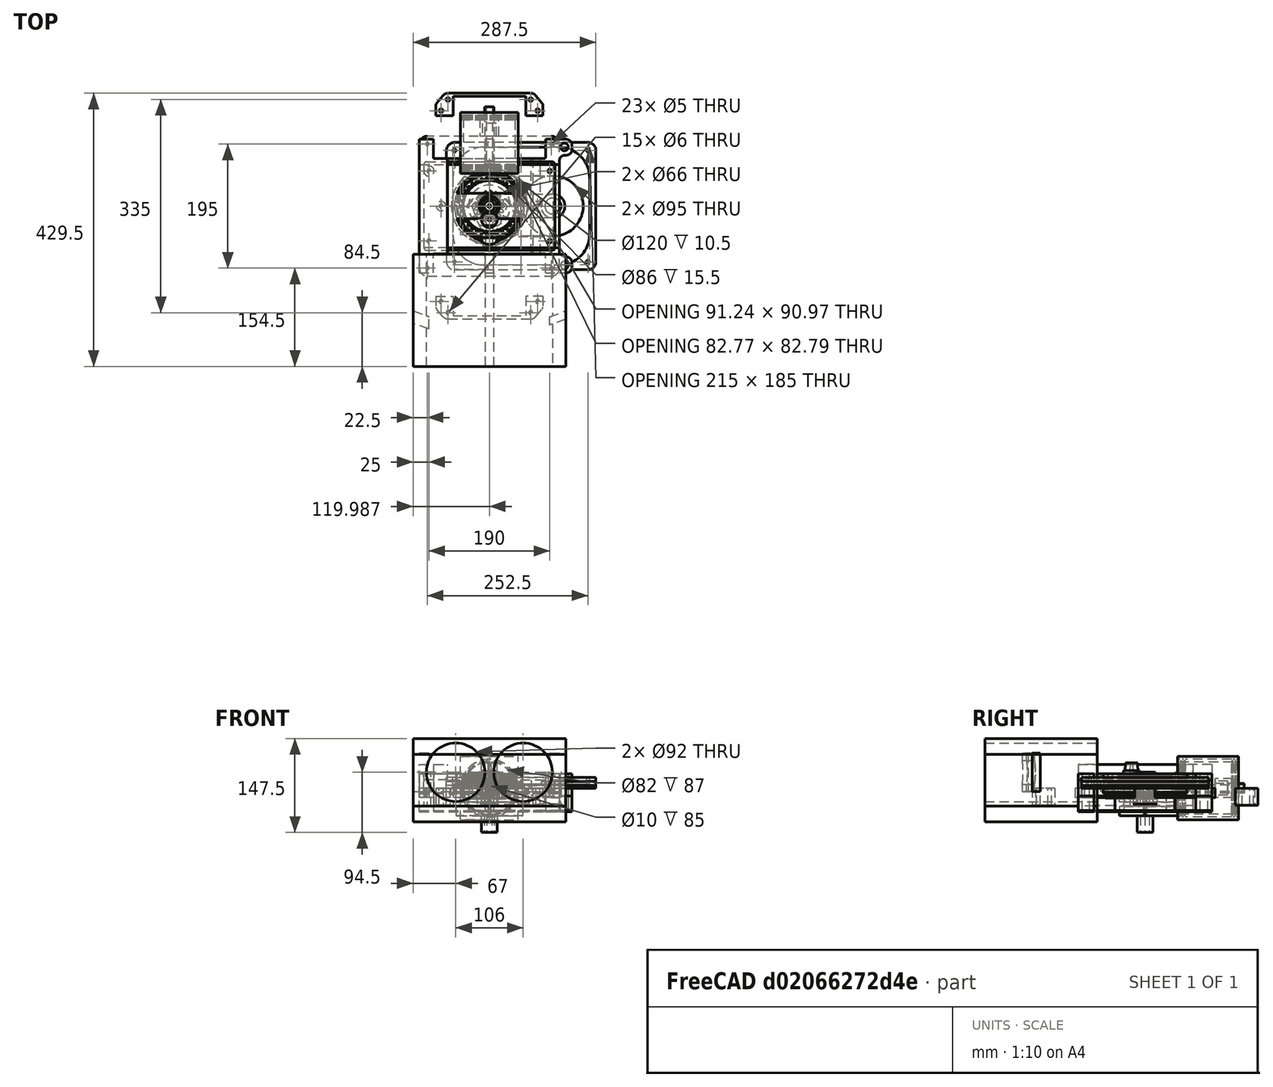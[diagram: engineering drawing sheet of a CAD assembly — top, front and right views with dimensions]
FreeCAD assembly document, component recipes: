
FREECAD ASSEMBLY — COMPONENT RECIPES ("assm4_X_at_Tusi_stirling")

This assembly document has 31 components, labeled P0..P30 below (a component is one placed body or linked part). 30 of them carry a construction recipe — the FreeCAD feature program that regenerates the part from scratch, quoted from this document or its linked companion documents; the rest are supplied as boundary geometry only. No exploded tour is included for this assembly.
COMPONENT P0 — geometry summary ("Assembly_total"; no construction recipe available for this part):
  bounding box: 312.0 x 312.0 x 138.0 mm
  tessellated surface: 110,152 triangles
  volume: 555531 mm^3 (4% of its bounding box)
  symmetry: mirror-symmetric across its x mid-plane
COMPONENT P1 — recipe-attached ("Шток_поршня", modeled in this document).
Construction recipe (the document's own serialized feature program — sketch geometry with constraints, then the solid features built on it; lengths are millimeters unless a unit is written):

FEATURE [PartDesign::CoordinateSystem] Pin
  AttacherType = Attacher::AttachEngine3D
  AttachmentSupport = -> [XY_Plane001]
  MapMode = 5
FEATURE [Sketcher::SketchObject] Sketch053
  ArcFitTolerance = 0
  AttachmentOffset = pos=(0,0,-66) rot=(0,0,1;0rad)
  AttachmentSupport = -> [XZ_Plane001]
  FullyConstrained = true
  MakeInternals = false
  MapMode = 5
  Placement = pos=(0,66,-1.47e-14) rot=(1,0,0;1.5708rad)
  sketch-geometry (2):
    g0: Circle CenterX=0 CenterY=0 CenterZ=0 NormalX=0 NormalY=0 NormalZ=1 AngleXU=0 Radius=7.5
    g1: Circle CenterX=0 CenterY=0 CenterZ=0 NormalX=0 NormalY=0 NormalZ=1 AngleXU=0 Radius=5
  constraints (4):
    c: Coincident(g0,g-1)
    c: Coincident(g1,g0)
    c: Diameter(g0) = 15
    c: Diameter(g1) = 10
FEATURE [PartDesign::Pad] Pad
  Direction = (0,-1,2e-16)
  Length = 90
  Length2 = 1
  Placement = pos=(0,0,0) rot=(1,0,0;1.5708rad)
  Profile = -> Sketch053
  ReferenceAxis = -> Sketch053 [N_Axis]
  Reversed = true
  Suppressed = false
  Type = 0
FEATURE [Sketcher::SketchObject] Sketch055
  ArcFitTolerance = 0
  AttachmentOffset = pos=(0,0,-66) rot=(0,0,1;0rad)
  AttachmentSupport = -> [XZ_Plane001]
  FullyConstrained = true
  MakeInternals = false
  MapMode = 5
  Placement = pos=(0,66,-1.47e-14) rot=(1,0,0;1.5708rad)
  sketch-geometry (2):
    g0: Circle CenterX=0 CenterY=0 CenterZ=0 NormalX=0 NormalY=0 NormalZ=1 AngleXU=0 Radius=5
    g1: Circle CenterX=0 CenterY=0 CenterZ=0 NormalX=0 NormalY=0 NormalZ=1 AngleXU=0 Radius=2
  constraints (4):
    c: Diameter(g0) = 10
    c: Coincident(g1,g0)
    c: Coincident(g0,g-1)
    c: Diameter(g1) = 4
FEATURE [PartDesign::Pad] Pad026
  BaseFeature = -> Pad
  Direction = (0,-1,2e-16)
  Length = 5
  Length2 = 17
  Placement = pos=(0,0,0) rot=(1,0,0;1.5708rad)
  Profile = -> Sketch055
  ReferenceAxis = -> Sketch055 [N_Axis]
  Reversed = true
  Suppressed = false
  Type = 4
FEATURE [Sketcher::SketchObject] Sketch085
  ArcFitTolerance = 1e-06
  AttachmentOffset = pos=(0,0,-66) rot=(0,0,1;0rad)
  AttachmentSupport = -> [XZ_Plane001]
  ExternalGeometry = -> [Pad026]
  FullyConstrained = true
  MakeInternals = false
  MapMode = 5
  Placement = pos=(0,66,-1.47e-14) rot=(1,0,0;1.5708rad)
  sketch-geometry (7):
    g0: ArcOfCircle CenterX=0 CenterY=0 CenterZ=0 NormalX=0 NormalY=0 NormalZ=1 AngleXU=0 Radius=7.5 StartAngle=2.41186 EndAngle=3.87132
    g1: LineSegment StartX=-5.59017 StartY=5 StartZ=0 EndX=5.59017 EndY=5 EndZ=0
    g2: LineSegment StartX=-5.59017 StartY=-5 StartZ=0 EndX=5.59017 EndY=-5 EndZ=0
    g3: ArcOfCircle CenterX=0 CenterY=0 CenterZ=0 NormalX=0 NormalY=0 NormalZ=1 AngleXU=0 Radius=7.5 StartAngle=5.55346 EndAngle=7.01291
    g4: LineSegment [constr] StartX=0 StartY=5 StartZ=0 EndX=0 EndY=-5 EndZ=0
    g5: LineSegment [constr] StartX=5.59017 StartY=5 StartZ=0 EndX=5.59017 EndY=-5 EndZ=0
    g6: Circle CenterX=0 CenterY=0 CenterZ=0 NormalX=0 NormalY=0 NormalZ=1 AngleXU=0 Radius=2
  constraints (20):
    c: Coincident(g0,g-1)
    c: Horizontal(g1)
    c: Horizontal(g2)
    c: Coincident(g0,g1)
    c: Coincident(g1,g3)
    c: Equal(g0,g3)
    c: Coincident(g0,g2)
    c: Coincident(g0,g3)
    c: Equal(g3,g-3)
    c: PointOnObject(g4,g-5)
    c: PointOnObject(g4,g-5)
    c: Coincident(g5,g1)
    c: Coincident(g5,g2)
    c: Vertical(g5)
    c: Equal(g4,g5)
    c: PointOnObject(g4,g-2)
    c: Coincident(g6,g0)
    c: Equal(g6,g-4)
    c: Coincident(g2,g3)
    c: Vertical(g4)
FEATURE [PartDesign::Pad] Pad046
  BaseFeature = -> Pad026
  Direction = (0,-1,2e-16)
  Length = 2
  Length2 = 10
  Placement = pos=(0,0,0) rot=(1,0,0;1.5708rad)
  Profile = -> Sketch085
  ReferenceAxis = -> Sketch085 [N_Axis]
  Refine = true
  Suppressed = false
  Type = 0
FEATURE [PartDesign::Body] Body  label="Шток_поршня"
  AllowCompound = false
  Group = -> [Pin,Sketch053,Pad,Sketch055,Pad026,Sketch085,Pad046]
  Origin = -> Origin001
  Tip = -> Pad046
COMPONENT P2 — recipe-attached ("Эксцентрик", modeled in this document).
Construction recipe (the document's own serialized feature program — sketch geometry with constraints, then the solid features built on it; lengths are millimeters unless a unit is written):

FEATURE [Sketcher::SketchObject] Sketch005
  ArcFitTolerance = 0
  AttachmentSupport = -> [XY_Plane002]
  FullyConstrained = true
  MakeInternals = false
  MapMode = 5
  expr: Constraints[1] = <<Dim_table>>.crank_dia2 + <<Dim_table>>.zazor
  expr: Constraints[26] = 10
  expr: Constraints[27] = <<Dim_table>>.ecc_dia * 0.8
  expr: Constraints[28] = <<Dim_table>>.crank_dia2 * 2
  expr: Constraints[2] = <<Dim_table>>.ecc_dia + <<Dim_table>>.roller_dia
  expr: Constraints[3] = <<Dim_table>>.crank_len
  sketch-geometry (14):
    g0: Circle CenterX=0 CenterY=-21.25 CenterZ=0 NormalX=0 NormalY=0 NormalZ=1 AngleXU=0 Radius=41.5
    g1: Circle CenterX=0 CenterY=0 CenterZ=0 NormalX=0 NormalY=0 NormalZ=1 AngleXU=0 Radius=12.75
    g2: ArcOfCircle CenterX=0 CenterY=-21.25 CenterZ=0 NormalX=0 NormalY=0 NormalZ=1 AngleXU=0 Radius=32 StartAngle=3.32205 EndAngle=4.38515
    g3: ArcOfCircle CenterX=0 CenterY=-21.25 CenterZ=0 NormalX=0 NormalY=0 NormalZ=1 AngleXU=0 Radius=32 StartAngle=5.03963 EndAngle=6.10273
    g4: LineSegment StartX=-5 StartY=-27.5681 StartZ=0 EndX=-5 EndY=-47.7641 EndZ=0
    g5: LineSegment StartX=5 StartY=-27.5681 StartZ=0 EndX=5 EndY=-47.7641 EndZ=0
    g6: ArcOfCircle CenterX=0 CenterY=0 CenterZ=0 NormalX=0 NormalY=0 NormalZ=1 AngleXU=0 Radius=25 StartAngle=3.98424 EndAngle=4.39683
    g7: ArcOfCircle CenterX=0 CenterY=0 CenterZ=0 NormalX=0 NormalY=0 NormalZ=1 AngleXU=0 Radius=25 StartAngle=5.02794 EndAngle=5.44053
    g8: ArcOfCircle CenterX=-22.6265 CenterY=-25.3779 CenterZ=0 NormalX=0 NormalY=0 NormalZ=1 AngleXU=0 Radius=9 StartAngle=0.842651 EndAngle=3.32205
    g9: ArcOfCircle CenterX=22.6265 CenterY=-25.3779 CenterZ=0 NormalX=0 NormalY=0 NormalZ=1 AngleXU=0 Radius=9 StartAngle=6.10273 EndAngle=8.58213
    g10: ArcOfCircle CenterX=-9 CenterY=-47.7641 CenterZ=0 NormalX=0 NormalY=0 NormalZ=1 AngleXU=0 Radius=4 StartAngle=4.38515 EndAngle=6.28319
    g11: ArcOfCircle CenterX=9 CenterY=-47.7641 CenterZ=0 NormalX=0 NormalY=0 NormalZ=1 AngleXU=0 Radius=4 StartAngle=3.14159 EndAngle=5.03963
    g12: ArcOfCircle CenterX=-9 CenterY=-27.5681 CenterZ=0 NormalX=0 NormalY=0 NormalZ=1 AngleXU=0 Radius=4 StartAngle=0 EndAngle=1.25524
    g13: ArcOfCircle CenterX=9 CenterY=-27.5681 CenterZ=0 NormalX=0 NormalY=0 NormalZ=1 AngleXU=0 Radius=4 StartAngle=1.88635 EndAngle=3.14159
  constraints (32):
    c: PointOnObject(g0,g-2)
    c: Diameter(g1) = 25.5
    c: Diameter(g0) = 83
    c: Distance(g1,g0) = 21.25
    c: Coincident(g1,g-1)
    c: Coincident(g2,g0)
    c: Coincident(g3,g0)
    c: Equal(g2,g3)
    c: Vertical(g4)
    c: Coincident(g6,g1)
    c: Coincident(g7,g1)
    c: Tangent(g2,g8) = -1.5708
    c: Tangent(g6,g8) = 1.5708
    c: Tangent(g7,g9) = 1.5708
    c: Tangent(g3,g9) = -1.5708
    c: Tangent(g2,g10) = -1.5708
    c: Tangent(g4,g10) = 1.5708
    c: Tangent(g5,g11) = -1.5708
    c: Tangent(g3,g11) = -1.5708
    c: Tangent(g6,g12) = 1.5708
    c: Tangent(g4,g12) = 1.5708
    c: Tangent(g5,g13) = -1.5708
    c: Tangent(g7,g13) = 1.5708
    c: Symmetric(g12,g13,g-2)
    c: Symmetric(g10,g11,g-2)
    c: Symmetric(g8,g9,g-2)
    c: DistanceX(g4,g5) = 10
    c: Diameter(g2) = 64
    c: Diameter(g6) = 50
    c: Radius(g10) = 4
    c: Equal(g10,g12)
    c: Radius(g8) = 9
FEATURE [PartDesign::CoordinateSystem] Eccentr
  AttacherType = Attacher::AttachEngine3D
  AttachmentOffset = pos=(0,0,0) rot=(0,0,1;1.5708rad)
  AttachmentSupport = -> [Sketch005]
  MapMode = 11
  Placement = pos=(0,0,0) rot=(0,0,1;3.14159rad)
FEATURE [PartDesign::Pad] Pad001
  Direction = (0,0,1)
  Length = 16.5
  Length2 = 0
  Profile = -> Sketch005
  ReferenceAxis = -> Sketch005 [N_Axis]
  Reversed = true
  Suppressed = false
  Type = 0
  expr: Length = <<Dim_table>>.ecc_hei
FEATURE [PartDesign::SubtractiveCylinder] Cylinder003
  Angle = 360
  AttacherType = Attacher::AttachEngine3D
  AttachmentOffset = pos=(0,0,-12.5) rot=(0,0,1;0rad)
  AttachmentSupport = -> [Pad001]
  BaseFeature = -> Pad001
  FirstAngle = 0
  Height = 25.2
  MapMode = 2
  Placement = pos=(0,0,-12.5) rot=(0,0,1;0rad)
  Radius = 16
  Refine = true
  SecondAngle = 0
  Suppressed = false
FEATURE [PartDesign::SubtractiveCylinder] Cylinder008
  Angle = 360
  AttacherType = Attacher::AttachEngine3D
  AttachmentOffset = pos=(23,0,-13) rot=(0,0,1;0rad)
  AttachmentSupport = -> [XY_Plane002]
  BaseFeature = -> Cylinder003
  FirstAngle = 0
  Height = 25
  MapMode = 5
  Placement = pos=(23,0,-13) rot=(0,0,1;0rad)
  Radius = 4
  Refine = true
  SecondAngle = 0
  Suppressed = false
FEATURE [PartDesign::SubtractiveCylinder] Cylinder009
  Angle = 360
  AttacherType = Attacher::AttachEngine3D
  AttachmentOffset = pos=(-23,0,-13) rot=(0,0,1;0rad)
  AttachmentSupport = -> [XY_Plane002]
  BaseFeature = -> Cylinder008
  FirstAngle = 0
  Height = 25
  MapMode = 5
  Placement = pos=(-23,0,-13) rot=(0,0,1;0rad)
  Radius = 4
  Refine = true
  SecondAngle = 0
  Suppressed = false
FEATURE [Sketcher::SketchObject] Sketch084
  ArcFitTolerance = 1e-06
  AttachmentSupport = -> [XY_Plane002]
  FullyConstrained = true
  MakeInternals = false
  MapMode = 5
  expr: Constraints[2] = <<Dim_table>>.crank_len
  expr: Constraints[3] = <<Dim_table>>.ecc_dia
  expr: Constraints[4] = <<Dim_table>>.ecc_dia * 1.2
  sketch-geometry (2):
    g0: Circle CenterX=0 CenterY=-21.25 CenterZ=0 NormalX=0 NormalY=0 NormalZ=1 AngleXU=0 Radius=40
    g1: Circle CenterX=0 CenterY=-21.25 CenterZ=0 NormalX=0 NormalY=0 NormalZ=1 AngleXU=0 Radius=48
  constraints (5):
    c: PointOnObject(g0,g-2)
    c: Coincident(g1,g0)
    c: Distance(g0,g-1) = 21.25
    c: Diameter(g0) = 80
    c: Diameter(g1) = 96
FEATURE [PartDesign::Pocket] Pocket
  BaseFeature = -> Cylinder009
  Direction = (0,0,-1)
  Length = 15.25
  Length2 = -1.25
  Placement = pos=(-23,0,-13) rot=(0,0,1;0rad)
  Profile = -> Sketch084
  ReferenceAxis = -> Sketch084 [N_Axis]
  Refine = true
  Suppressed = false
  Type = 4
FEATURE [PartDesign::Body] Body001  label="Эксцентрик"
  AllowCompound = false
  Group = -> [Sketch005,Pad001,Eccentr,Cylinder003,Cylinder008,Cylinder009,Sketch084,Pocket]
  Origin = -> Origin002
  Tip = -> Pocket
COMPONENT P3 — recipe-attached ("Ползун_рабочий", modeled in this document).
Construction recipe (the document's own serialized feature program — sketch geometry with constraints, then the solid features built on it; lengths are millimeters unless a unit is written):

FEATURE [Sketcher::SketchObject] Sketch007
  ArcFitTolerance = 0
  AttachmentSupport = -> [XY_Plane003]
  FullyConstrained = true
  MakeInternals = false
  MapMode = 5
  expr: Constraints[15] = <<Dim_table>>.ecc_dia * 1.3
  expr: Constraints[17] = <<Dim_table>>.ecc_dia * 0.8
  expr: Constraints[1] = <<Dim_table>>.ecc_dia + 2 * <<Dim_table>>.roller_dia
  sketch-geometry (15):
    g0: Circle CenterX=0 CenterY=0 CenterZ=0 NormalX=0 NormalY=0 NormalZ=1 AngleXU=0 Radius=43
    g1: ArcOfCircle CenterX=0 CenterY=0 CenterZ=0 NormalX=0 NormalY=0 NormalZ=1 AngleXU=0 Radius=52 StartAngle=1.86916 EndAngle=3.14159
    g2: ArcOfCircle CenterX=0 CenterY=0 CenterZ=0 NormalX=0 NormalY=0 NormalZ=1 AngleXU=0 Radius=52 StartAngle=0 EndAngle=1.27243
    g3: LineSegment StartX=-11.8314 StartY=53.6134 StartZ=0 EndX=-10 EndY=64 EndZ=0
    g4: LineSegment StartX=-10 StartY=64 StartZ=0 EndX=10 EndY=64 EndZ=0
    g5: LineSegment StartX=10 StartY=64 StartZ=0 EndX=11.8314 EndY=53.6134 EndZ=0
    g6: ArcOfCircle CenterX=-16.7555 CenterY=54.4817 CenterZ=0 NormalX=0 NormalY=0 NormalZ=1 AngleXU=0 Radius=5 StartAngle=5.01075 EndAngle=6.10865
    g7: ArcOfCircle CenterX=16.7555 CenterY=54.4817 CenterZ=0 NormalX=0 NormalY=0 NormalZ=1 AngleXU=0 Radius=5 StartAngle=3.31613 EndAngle=4.41403
    g8: ArcOfCircle CenterX=-2.7e-15 CenterY=2.94305e-05 CenterZ=0 NormalX=0 NormalY=0 NormalZ=1 AngleXU=0 Radius=52 StartAngle=3.14159 EndAngle=4.41403
    g9: ArcOfCircle CenterX=-16.7555 CenterY=-54.4817 CenterZ=0 NormalX=0 NormalY=0 NormalZ=1 AngleXU=0 Radius=5 StartAngle=0.174533 EndAngle=1.27243
    g10: LineSegment StartX=-11.8314 StartY=-53.6134 StartZ=0 EndX=-10 EndY=-64 EndZ=0
    g11: LineSegment StartX=-10 StartY=-64 StartZ=0 EndX=10 EndY=-64 EndZ=0
    g12: LineSegment StartX=10 StartY=-64 StartZ=0 EndX=11.8314 EndY=-53.6134 EndZ=0
    g13: ArcOfCircle CenterX=16.7555 CenterY=-54.4817 CenterZ=0 NormalX=0 NormalY=0 NormalZ=1 AngleXU=0 Radius=5 StartAngle=1.86916 EndAngle=2.96706
    g14: ArcOfCircle CenterX=-2.7e-15 CenterY=2.94305e-05 CenterZ=0 NormalX=0 NormalY=0 NormalZ=1 AngleXU=0 Radius=52 StartAngle=5.01075 EndAngle=6.28318
  constraints (36):
    c: Coincident(g0,g-1)
    c: Diameter(g0) = 86
    c: Coincident(g1,g0)
    c: Coincident(g2,g0)
    c: Equal(g1,g2)
    c: Coincident(g3,g4)
    c: Coincident(g4,g5)
    c: Tangent(g1,g6) = 1.5708
    c: Tangent(g3,g6) = -1.5708
    c: Tangent(g5,g7) = -1.5708
    c: Tangent(g2,g7) = 1.5708
    c: Symmetric(g6,g7,g-2)
    c: Symmetric(g3,g4,g-2)
    c: PointOnObject(g1,g-1)
    c: PointOnObject(g2,g-1)
    c: Diameter(g1) = 104
    c: Distance(g4,g4) = 20
    c: DistanceY(g0,g4) = 64
    c: Radius(g6) = 5
    c: Angle(g3,g-2) = 0.174533
    c: Equal(g8,g14)
    c: Coincident(g10,g11)
    c: Coincident(g11,g12)
    c: Tangent(g8,g9) = 1.5708
    c: Tangent(g10,g9) = 1.5708
    c: Tangent(g12,g13) = 1.5708
    c: Tangent(g14,g13) = 1.5708
    c: Equal(g8,g1)
    c: Equal(g13,g7)
    c: Symmetric(g9,g13,g-2)
    c: Symmetric(g11,g4,g-1)
    c: Symmetric(g10,g11,g-2)
    c: Parallel(g12,g3)
    c: Coincident(g8,g1)
    c: Coincident(g14,g2)
    c: Coincident(g8,g14)
FEATURE [PartDesign::Pad] Pad002
  Direction = (0,0,1)
  Length = 15.5
  Length2 = 10
  Midplane = true
  Profile = -> Sketch007
  ReferenceAxis = -> Sketch007 [N_Axis]
  Suppressed = false
  Type = 0
  expr: Length = <<Dim_table>>.ecc_hei - 1
FEATURE [PartDesign::CoordinateSystem] Shtok
  AttacherType = Attacher::AttachEngine3D
  AttachmentSupport = -> [Pad002]
  MapMode = 45
  Placement = pos=(-7.2e-15,2.69855e-05,-3e-16) rot=(0,0,1;0rad)
FEATURE [Sketcher::SketchObject] Sketch
  ArcFitTolerance = 1e-06
  AttachmentSupport = -> [Pad002]
  FullyConstrained = true
  MakeInternals = false
  MapMode = 5
  Placement = pos=(0,-64,0) rot=(1,0,0;1.5708rad)
  sketch-geometry (1):
    g0: Circle CenterX=0 CenterY=0 CenterZ=0 NormalX=0 NormalY=0 NormalZ=1 AngleXU=0 Radius=0.5
  constraints (2):
    c: Coincident(g0,g-1)
    c: Diameter(g0) = 1
FEATURE [PartDesign::Hole] Hole001
  BaseFeature = -> Pad002
  CustomThreadClearance = 0
  Depth = 15
  DepthType = 0
  Diameter = 11
  DrillForDepth = false
  DrillPoint = 1
  DrillPointAngle = 118
  HoleCutCountersinkAngle = 90
  HoleCutCustomValues = false
  HoleCutDepth = 0
  HoleCutDiameter = 6.1
  HoleCutType = 0
  ModelThread = false
  Profile = -> Sketch
  Refine = true
  Suppressed = false
  Tapered = false
  TaperedAngle = 90
  ThreadClass = 0
  ThreadDepth = 15
  ThreadDepthType = 0
  ThreadDirection = 0
  ThreadFit = 0
  ThreadSize = 22
  ThreadType = 2
  Threaded = false
  UseCustomThreadClearance = false
FEATURE [Sketcher::SketchObject] Sketch083
  ArcFitTolerance = 1e-06
  AttachmentSupport = -> [Hole001]
  FullyConstrained = true
  MakeInternals = false
  MapMode = 5
  Placement = pos=(0,64,0) rot=(0,0.707107,0.707107;3.14159rad)
  sketch-geometry (1):
    g0: Circle CenterX=0 CenterY=0 CenterZ=0 NormalX=0 NormalY=0 NormalZ=1 AngleXU=0 Radius=0.5
  constraints (2):
    c: Coincident(g0,g-1)
    c: Diameter(g0) = 1
FEATURE [PartDesign::Hole] Hole002
  BaseFeature = -> Hole001
  CustomThreadClearance = 0
  Depth = 15
  DepthType = 0
  Diameter = 11
  DrillForDepth = false
  DrillPoint = 1
  DrillPointAngle = 118
  HoleCutCountersinkAngle = 90
  HoleCutCustomValues = false
  HoleCutDepth = 0
  HoleCutDiameter = 6.1
  HoleCutType = 0
  ModelThread = false
  Profile = -> Sketch083
  Refine = true
  Suppressed = false
  Tapered = false
  TaperedAngle = 90
  ThreadClass = 0
  ThreadDepth = 15
  ThreadDepthType = 0
  ThreadDirection = 0
  ThreadFit = 0
  ThreadSize = 22
  ThreadType = 2
  Threaded = false
  UseCustomThreadClearance = false
FEATURE [PartDesign::Body] Body002  label="Ползун_рабочий"
  AllowCompound = false
  Group = -> [Sketch007,Pad002,Shtok,Sketch,Hole001,Sketch083,Hole002]
  Origin = -> Origin003
  Tip = -> Hole002
COMPONENT P4 — recipe-attached ("Шейка_шатунная", modeled in this document).
Construction recipe (the document's own serialized feature program — sketch geometry with constraints, then the solid features built on it; lengths are millimeters unless a unit is written):

FEATURE [Sketcher::SketchObject] Sketch004
  ArcFitTolerance = 0
  AttachmentSupport = -> [XY_Plane004]
  FullyConstrained = true
  MakeInternals = false
  MapMode = 5
  expr: Constraints[0] = <<Dim_table>>.crank_dia2
  expr: Constraints[2] = <<Dim_table>>.crank_len
  expr: Constraints[4] = <<Dim_table>>.axle_hole_dia
  sketch-geometry (2):
    g0: Circle CenterX=0 CenterY=-21.25 CenterZ=0 NormalX=0 NormalY=0 NormalZ=1 AngleXU=0 Radius=12.5
    g1: Circle CenterX=0 CenterY=-21.25 CenterZ=0 NormalX=0 NormalY=0 NormalZ=1 AngleXU=0 Radius=2.5
  constraints (5):
    c: Diameter(g0) = 25
    c: PointOnObject(g0,g-2)
    c: DistanceY(g0,g-1) = 21.25
    c: Coincident(g1,g0)
    c: Diameter(g1) = 5
FEATURE [PartDesign::Pad] Pad003
  Direction = (0,0,1)
  Length = 63
  Length2 = 0
  Profile = -> Sketch004
  ReferenceAxis = -> Sketch004 [N_Axis]
  Suppressed = false
  Type = 0
FEATURE [Sketcher::SketchObject] Sketch070
  ArcFitTolerance = 0
  AttachmentSupport = -> [Pad003]
  FullyConstrained = true
  MakeInternals = false
  MapMode = 11
  Placement = pos=(0,-21.25,63) rot=(0,0,1;1.5708rad)
  expr: Constraints[12] = <<Dim_table>>.crank_dia2
  expr: Constraints[13] = <<Dim_table>>.axle_hole_dia
  expr: Constraints[14] = 0
  expr: Constraints[3] = <<Dim_table>>.crank_dia2 * 0.8
  sketch-geometry (5):
    g0: ArcOfCircle CenterX=0 CenterY=0 CenterZ=0 NormalX=0 NormalY=0 NormalZ=1 AngleXU=0 Radius=12.5 StartAngle=0.643501 EndAngle=2.49809
    g1: ArcOfCircle CenterX=0 CenterY=0 CenterZ=0 NormalX=0 NormalY=0 NormalZ=1 AngleXU=0 Radius=12.5 StartAngle=3.78509 EndAngle=5.63968
    g2: LineSegment StartX=10 StartY=7.5 StartZ=0 EndX=10 EndY=-7.5 EndZ=0
    g3: LineSegment StartX=-10 StartY=7.5 StartZ=0 EndX=-10 EndY=-7.5 EndZ=0
    g4: Circle CenterX=0 CenterY=0 CenterZ=0 NormalX=0 NormalY=0 NormalZ=1 AngleXU=0 Radius=2.5
  constraints (15):
    c: Coincident(g2,g0)
    c: Coincident(g2,g1)
    c: Vertical(g2)
    c: DistanceX(g0,g0) = 20
    c: Coincident(g3,g0)
    c: Coincident(g3,g1)
    c: Vertical(g3)
    c: Equal(g3,g2)
    c: Equal(g1,g0)
    c: Coincident(g1,g0)
    c: Coincident(g4,g0)
    c: PointOnObject(g0,g-2)
    c: Diameter(g0) = 25
    c: Diameter(g4) = 5
    c: DistanceY(g-1,g0) = 0
FEATURE [PartDesign::Pad] Pad038
  BaseFeature = -> Pad003
  Direction = (0,0,1)
  Length = 12
  Length2 = 10
  Profile = -> Sketch070
  ReferenceAxis = -> Sketch070 [N_Axis]
  Suppressed = false
  TaperAngle = -2
  Type = 0
FEATURE [PartDesign::Body] Body003  label="Шейка_шатунная"
  AllowCompound = false
  Group = -> [Sketch004,Pad003,Sketch070,Pad038]
  Origin = -> Origin004
  Placement = pos=(0,0,-25) rot=(0,0,1;0rad)
  Tip = -> Pad038
COMPONENT P5 — recipe-attached ("Щека", modeled in this document).
Construction recipe (the document's own serialized feature program — sketch geometry with constraints, then the solid features built on it; lengths are millimeters unless a unit is written):

FEATURE [Sketcher::SketchObject] Sketch003
  ArcFitTolerance = 0
  AttachmentSupport = -> [XY_Plane005]
  FullyConstrained = true
  MakeInternals = false
  MapMode = 5
  expr: Constraints[17] = <<Dim_table>>.fillet_r
  expr: Constraints[18] = <<Dim_table>>.fillet_r
  expr: Constraints[21] = <<Dim_table>>.inter_shaft_len - <<Dim_table>>.zazor
  expr: Constraints[23] = <<Dim_table>>.axle_hole_dia
  expr: Constraints[25] = 70
  expr: Constraints[26] = <<Dim_table>>.crank_dia2 * 1.5
  expr: Constraints[27] = <<Dim_table>>.crank_len
  sketch-geometry (14):
    g0: ArcOfCircle CenterX=0 CenterY=0 CenterZ=0 NormalX=0 NormalY=0 NormalZ=1 AngleXU=0 Radius=52.5 StartAngle=0.0396143 EndAngle=3.10198
    g1: ArcOfCircle CenterX=-1.2e-15 CenterY=-21.25 CenterZ=0 NormalX=0 NormalY=0 NormalZ=1 AngleXU=0 Radius=18.75 StartAngle=3.49066 EndAngle=5.93412
    g2: LineSegment [constr] StartX=-17.6192 StartY=-27.6629 StartZ=0 EndX=17.6192 EndY=-27.6629 EndZ=0
    g3: LineSegment StartX=-50.4604 StartY=0 StartZ=0 EndX=-29.0881 EndY=0 EndZ=0
    g4: LineSegment StartX=-27.2087 StartY=-1.31596 StartZ=0 EndX=-17.6192 EndY=-27.6629 EndZ=0
    g5: LineSegment StartX=17.6192 StartY=-27.6629 StartZ=0 EndX=27.2087 EndY=-1.31596 EndZ=0
    g6: LineSegment StartX=29.0881 StartY=-7e-16 StartZ=0 EndX=50.4604 EndY=-7e-16 EndZ=0
    g7: ArcOfCircle CenterX=-29.0881 CenterY=-2 CenterZ=0 NormalX=0 NormalY=0 NormalZ=1 AngleXU=0 Radius=2 StartAngle=0.349066 EndAngle=1.5708
    g8: ArcOfCircle CenterX=29.0881 CenterY=-2 CenterZ=0 NormalX=0 NormalY=0 NormalZ=1 AngleXU=0 Radius=2 StartAngle=1.5708 EndAngle=2.79253
    g9: ArcOfCircle CenterX=50.4604 CenterY=2 CenterZ=0 NormalX=0 NormalY=0 NormalZ=1 AngleXU=0 Radius=2 StartAngle=4.71239 EndAngle=6.3228
    g10: ArcOfCircle CenterX=-50.4604 CenterY=2 CenterZ=0 NormalX=0 NormalY=0 NormalZ=1 AngleXU=0 Radius=2 StartAngle=3.10198 EndAngle=4.71239
    g11: Circle [constr] CenterX=0 CenterY=0 CenterZ=0 NormalX=0 NormalY=0 NormalZ=1 AngleXU=0 Radius=49.75
    g12: Circle CenterX=0 CenterY=0 CenterZ=0 NormalX=0 NormalY=0 NormalZ=1 AngleXU=0 Radius=2.5
    g13: Circle [constr] CenterX=-1.2e-15 CenterY=-21.25 CenterZ=0 NormalX=0 NormalY=0 NormalZ=1 AngleXU=0 Radius=2.5
  constraints (31):
    c: Coincident(g2,g1)
    c: Coincident(g2,g1)
    c: Horizontal(g2)
    c: Horizontal(g3)
    c: Horizontal(g6)
    c: Tangent(g4,g1) = -1.5708
    c: Tangent(g5,g1) = -1.5708
    c: Tangent(g3,g7) = 1.5708
    c: Tangent(g4,g7) = 1.5708
    c: Tangent(g6,g8) = 1.5708
    c: Tangent(g5,g8) = 1.5708
    c: Tangent(g6,g9) = -1.5708
    c: Tangent(g0,g9) = -1.5708
    c: Tangent(g0,g10) = -1.5708
    c: Tangent(g3,g10) = -1.5708
    c: Symmetric(g7,g8,g-2)
    c: Symmetric(g10,g9,g-2)
    c: Radius(g10) = 2
    c: Radius(g7) = 2
    c: Coincident(g0,g-1)
    c: Coincident(g11,g0)
    c: Diameter(g11) = 99.5
    c: Coincident(g12,g11)
    c: Diameter(g12) = 5
    c: Diameter(g0) = 105
    c: Angle(g5) = 1.22173
    c: Diameter(g1) = 37.5
    c: DistanceY(g1,g12) = 21.25
    c: PointOnObject(g3,g-1)
    c: Coincident(g13,g1)
    c: Equal(g13,g12)
FEATURE [PartDesign::Pad] Pad004
  Direction = (0,0,1)
  Length = 15
  Length2 = 10
  Profile = -> Sketch003
  ReferenceAxis = -> Sketch003 [N_Axis]
  Suppressed = false
  Type = 0
FEATURE [PartDesign::Body] Body004  label="Щека"
  AllowCompound = false
  Group = -> [Sketch003,Pad004]
  Origin = -> Origin005
  Placement = pos=(0,0,12.5) rot=(0,0,1;0rad)
  Tip = -> Pad004
COMPONENT P6 — recipe-attached ("Шейка коренная", modeled in this document).
Construction recipe (the document's own serialized feature program — sketch geometry with constraints, then the solid features built on it; lengths are millimeters unless a unit is written):

FEATURE [Sketcher::SketchObject] Sketch002
  ArcFitTolerance = 0
  AttachmentSupport = -> [XY_Plane006]
  FullyConstrained = true
  MakeInternals = false
  MapMode = 5
  expr: Constraints[0] = <<Dim_table>>.crank_dia1
  expr: Constraints[20] = <<Dim_table>>.hex_size
  sketch-geometry (8):
    g0: Circle CenterX=0 CenterY=0 CenterZ=0 NormalX=0 NormalY=0 NormalZ=1 AngleXU=0 Radius=12.5
    g1: LineSegment StartX=4.04145 StartY=7 StartZ=0 EndX=-4.04145 EndY=7 EndZ=0
    g2: LineSegment StartX=-4.04145 StartY=7 StartZ=0 EndX=-8.0829 EndY=0 EndZ=0
    g3: LineSegment StartX=-8.0829 StartY=0 StartZ=0 EndX=-4.04145 EndY=-7 EndZ=0
    g4: LineSegment StartX=-4.04145 StartY=-7 StartZ=0 EndX=4.04145 EndY=-7 EndZ=0
    g5: LineSegment StartX=4.04145 StartY=-7 StartZ=0 EndX=8.0829 EndY=-9e-16 EndZ=0
    g6: LineSegment StartX=8.0829 StartY=-9e-16 StartZ=0 EndX=4.04145 EndY=7 EndZ=0
    g7: Circle [constr] CenterX=0 CenterY=0 CenterZ=0 NormalX=0 NormalY=0 NormalZ=1 AngleXU=0 Radius=8.0829
  constraints (18):
    c: Diameter(g0) = 25
    c: Coincident(g1,g2)
    c: Coincident(g2,g3)
    c: Coincident(g3,g4)
    c: Coincident(g4,g5)
    c: Coincident(g5,g6)
    c: Coincident(g6,g1)
    c: Equal(g1, g2-g6) x5
    c: PointOnObject(g1,g7)
    c: PointOnObject(g2,g7)
    c: PointOnObject(g3,g7)
    c: PointOnObject(g4,g7)
    c: PointOnObject(g5,g7)
    c: PointOnObject(g6,g7)
    c: Coincident(g7,g0)
    c: Horizontal(g1)
    c: DistanceY(g3,g1) = 14
    c: Coincident(g0,g-1)
FEATURE [PartDesign::Pad] Pad005
  Direction = (0,0,1)
  Length = 26
  Length2 = 10
  Profile = -> Sketch002
  ReferenceAxis = -> Sketch002 [N_Axis]
  Reversed = true
  Suppressed = false
  Type = 0
FEATURE [PartDesign::Body] Body005  label="Шейка коренная"
  AllowCompound = false
  Group = -> [Sketch002,Pad005]
  Origin = -> Origin006
  Placement = pos=(0,0,47) rot=(0,0,1;0rad)
  Tip = -> Pad005
COMPONENT P7 — recipe-attached ("Body052", modeled in this document).
Construction recipe (the document's own serialized feature program — sketch geometry with constraints, then the solid features built on it; lengths are millimeters unless a unit is written):

FEATURE [PartDesign::FeatureBase] Clone002
  BaseFeature = -> Body003
  Suppressed = false
FEATURE [PartDesign::Body] Body052
  AllowCompound = false
  Group = -> [Clone002]
  Origin = -> Origin053
  Placement = pos=(0,0,-35.5) rot=(0,0,1;0rad)
  Tip = -> Clone002
COMPONENT P8 — recipe-attached ("Body054", modeled in this document).
Construction recipe (the document's own serialized feature program — sketch geometry with constraints, then the solid features built on it; lengths are millimeters unless a unit is written):

FEATURE [PartDesign::FeatureBase] Clone004
  BaseFeature = -> Body005
  Suppressed = false
FEATURE [PartDesign::Body] Body054
  AllowCompound = false
  Group = -> [Clone004]
  Origin = -> Origin055
  Placement = pos=(0,0,-43.5) rot=(0,0,1;0rad)
  Tip = -> Clone004
COMPONENT P9 — recipe-attached ("Body055", modeled in this document).
Construction recipe (the document's own serialized feature program — sketch geometry with constraints, then the solid features built on it; lengths are millimeters unless a unit is written):

FEATURE [PartDesign::FeatureBase] Clone005
  BaseFeature = -> Body004
  Suppressed = false
FEATURE [PartDesign::Body] Body055
  AllowCompound = false
  Group = -> [Clone005]
  Origin = -> Origin056
  Placement = pos=(0,0,-43.5) rot=(0,0,1;0rad)
  Tip = -> Clone005
COMPONENT P10 — recipe-attached ("Колевал (секция)", modeled in this document).
Construction recipe (the document's own serialized feature program — sketch geometry with constraints, then the solid features built on it; lengths are millimeters unless a unit is written):

FEATURE [PartDesign::FeatureBase] Clone007
  BaseFeature = -> Fusion
  Suppressed = false
FEATURE [PartDesign::CoordinateSystem] Crank_shaft
  AttacherType = Attacher::AttachEngine3D
  AttachmentSupport = -> [Clone007]
  MapMode = 11
  Placement = pos=(0,0,-28.5) rot=(0,0,1;1.5708rad)
FEATURE [PartDesign::Fillet] Fillet
  Base = -> Clone007 [Edge52,Edge1]
  BaseFeature = -> Clone007
  Radius = 0.25
  Refine = true
  SupportTransform = false
  Suppressed = false
  UseAllEdges = false
FEATURE [PartDesign::Body] Body057  label="Колевал (секция)"
  AllowCompound = false
  Group = -> [Clone007,Crank_shaft,Fillet]
  Origin = -> Origin058
  Tip = -> Fillet
COMPONENT P11 — recipe-attached ("перегородка", modeled in this document).
Construction recipe (the document's own serialized feature program — sketch geometry with constraints, then the solid features built on it; lengths are millimeters unless a unit is written):

FEATURE [Sketcher::SketchObject] Sketch021
  ArcFitTolerance = 0
  AttachmentSupport = -> [XY_Plane062]
  FullyConstrained = false
  MakeInternals = false
  MapMode = 5
  sketch-geometry (30):
    g0: LineSegment [constr] StartX=-110 StartY=225 StartZ=0 EndX=110 EndY=225 EndZ=0
    g1: LineSegment [constr] StartX=110 StartY=225 StartZ=0 EndX=110 EndY=-225 EndZ=0
    g2: LineSegment [constr] StartX=110 StartY=-225 StartZ=0 EndX=-110 EndY=-225 EndZ=0
    g3: LineSegment [constr] StartX=-110 StartY=-225 StartZ=0 EndX=-110 EndY=225 EndZ=0
    g4: LineSegment [constr] StartX=-110 StartY=225 StartZ=0 EndX=-110 EndY=105 EndZ=0
    g5: LineSegment [constr] StartX=-110 StartY=105 StartZ=0 EndX=110 EndY=105 EndZ=0
    g6: LineSegment [constr] StartX=110 StartY=105 StartZ=0 EndX=110 EndY=225 EndZ=0
    g7: LineSegment [constr] StartX=-110 StartY=-225 StartZ=0 EndX=-110 EndY=-105 EndZ=0
    g8: LineSegment StartX=-110 StartY=-105 StartZ=0 EndX=110 EndY=-105 EndZ=0
    g9: LineSegment [constr] StartX=110 StartY=-105 StartZ=0 EndX=110 EndY=-225 EndZ=0
    g10: LineSegment [constr] StartX=-110 StartY=-105 StartZ=0 EndX=-110 EndY=105 EndZ=0
    g11: LineSegment StartX=110 StartY=105 StartZ=0 EndX=-110 EndY=105 EndZ=0
    g12: Circle CenterX=0 CenterY=0 CenterZ=0 NormalX=0 NormalY=0 NormalZ=1 AngleXU=0 Radius=33
    g13: LineSegment StartX=-110 StartY=105 StartZ=0 EndX=-110 EndY=0 EndZ=0
    g14: LineSegment [constr] StartX=110 StartY=-105 StartZ=0 EndX=110 EndY=105 EndZ=0
    g15: LineSegment StartX=110 StartY=105 StartZ=0 EndX=120.902 EndY=105 EndZ=0
    g16: LineSegment StartX=130 StartY=95.9016 StartZ=0 EndX=130 EndY=89.0984 EndZ=0
    g17: LineSegment StartX=120.902 StartY=80 StartZ=0 EndX=119.098 EndY=80 EndZ=0
    g18: ArcOfCircle CenterX=120.902 CenterY=95.9016 CenterZ=0 NormalX=0 NormalY=0 NormalZ=1 AngleXU=0 Radius=9.09838 StartAngle=0 EndAngle=1.5708
    g19: ArcOfCircle CenterX=120.902 CenterY=89.0984 CenterZ=0 NormalX=0 NormalY=0 NormalZ=1 AngleXU=0 Radius=9.09838 StartAngle=4.71239 EndAngle=6.28319
    g20: LineSegment StartX=110 StartY=70.9016 StartZ=0 EndX=110 EndY=0 EndZ=0
    g21: ArcOfCircle CenterX=119.098 CenterY=70.9016 CenterZ=0 NormalX=0 NormalY=0 NormalZ=1 AngleXU=0 Radius=9.09838 StartAngle=1.5708 EndAngle=3.14159
    g22: LineSegment StartX=110 StartY=-105 StartZ=0 EndX=120.902 EndY=-105 EndZ=0
    g23: LineSegment StartX=130 StartY=-95.9016 StartZ=0 EndX=130 EndY=-89.0984 EndZ=0
    g24: LineSegment StartX=120.902 StartY=-80 StartZ=0 EndX=119.098 EndY=-80 EndZ=0
    g25: ArcOfCircle CenterX=120.902 CenterY=-95.9016 CenterZ=0 NormalX=0 NormalY=0 NormalZ=1 AngleXU=0 Radius=9.09838 StartAngle=4.71239 EndAngle=6.28319
    g26: ArcOfCircle CenterX=120.902 CenterY=-89.0984 CenterZ=0 NormalX=0 NormalY=0 NormalZ=1 AngleXU=0 Radius=9.09838 StartAngle=0 EndAngle=1.5708
    g27: LineSegment StartX=110 StartY=-70.9016 StartZ=0 EndX=110 EndY=0 EndZ=0
    g28: ArcOfCircle CenterX=119.098 CenterY=-70.9016 CenterZ=0 NormalX=0 NormalY=0 NormalZ=1 AngleXU=0 Radius=9.09838 StartAngle=3.14159 EndAngle=4.71239
    g29: LineSegment StartX=-110 StartY=-105 StartZ=0 EndX=-110 EndY=0 EndZ=0
  constraints (61):
    c: Coincident(g0,g1)
    c: Coincident(g1,g2)
    c: Coincident(g2,g3)
    c: Coincident(g3,g0)
    c: Horizontal(g2)
    c: Vertical(g1)
    c: Symmetric(g0,g0,g-2)
    c: Symmetric(g0,g2,g-1)
    c: Coincident(g0,g4)
    c: PointOnObject(g4,g3)
    c: Coincident(g4,g5)
    c: PointOnObject(g5,g1)
    c: Horizontal(g5)
    c: Coincident(g6,g0)
    c: Coincident(g2,g7)
    c: PointOnObject(g7,g3)
    c: Horizontal(g8)
    c: Coincident(g9,g2)
    c: Equal(g9,g6)
    c: DistanceX(g2,g2) = 220
    c: DistanceY(g3,g3) = 450
    c: DistanceY(g9,g9) = 120
    c: Coincident(g10,g4)
    c: Coincident(g11,g10)
    c: Diameter(g12) = 66
    c: PointOnObject(g13,g-1)
    c: Vertical(g13)
    c: Vertical(g10)
    c: Vertical(g6)
    c: Coincident(g8,g9)
    c: Coincident(g8,g7)
    c: Coincident(g11,g5)
    c: Symmetric(g8,g11,g-1)
    c: Horizontal(g15)
    c: Horizontal(g17)
    c: Vertical(g16)
    c: Tangent(g15,g18) = 1.5708
    c: Tangent(g16,g18) = 1.5708
    c: Tangent(g16,g19) = 1.5708
    c: Tangent(g17,g19) = 1.5708
    c: Equal(g19,g18)
    c: Vertical(g20)
    c: Tangent(g17,g21) = -1.5708
    c: Tangent(g20,g21) = -1.5708
    c: Equal(g19,g21)
    c: Vertical(g14)
    c: Horizontal(g22)
    c: Horizontal(g24)
    c: Vertical(g23)
    c: Tangent(g22,g25) = -1.5708
    c: Tangent(g23,g25) = -1.5708
    c: Tangent(g23,g26) = -1.5708
    c: Tangent(g24,g26) = -1.5708
    c: Equal(g26,g25)
    c: Vertical(g27)
    c: Tangent(g24,g28) = 1.5708
    c: Tangent(g27,g28) = 1.5708
    c: Equal(g26,g28)
    c: Coincident(g13,g11)
    c: Coincident(g29,g8)
    c: Coincident(g29,g13)
FEATURE [Sketcher::SketchObject] Sketch022
  ArcFitTolerance = 0
  AttachmentSupport = -> [XY_Plane062]
  FullyConstrained = true
  MakeInternals = false
  MapMode = 5
  sketch-geometry (5):
    g0: LineSegment StartX=-110 StartY=-105 StartZ=0 EndX=-65.5 EndY=-105 EndZ=0
    g1: LineSegment StartX=-65.5 StartY=-105 StartZ=0 EndX=-65.5 EndY=105 EndZ=0
    g2: LineSegment StartX=-65.5 StartY=105 StartZ=0 EndX=-110 EndY=105 EndZ=0
    g3: LineSegment StartX=-110 StartY=105 StartZ=0 EndX=-110 EndY=-105 EndZ=0
    g4: LineSegment [constr] StartX=65.5 StartY=52.9337 StartZ=0 EndX=65.5 EndY=105 EndZ=0
  constraints (14):
    c: Coincident(g0,g1)
    c: Coincident(g1,g2)
    c: Coincident(g2,g3)
    c: Coincident(g3,g0)
    c: Horizontal(g0)
    c: Horizontal(g2)
    c: Vertical(g3)
    c: Vertical(g4)
    c: DistanceX(g1,g4) = 131
    c: Symmetric(g1,g4,g-2)
    c: DistanceY(g1,g1) = 210
    c: DistanceX(g0,g0) = 44.5
    c: Symmetric(g0,g1,g-1)
    c: Block(g4)
FEATURE [PartDesign::Pad] Pad012
  Direction = (0,0,1)
  Length = 35
  Length2 = 12.5
  Profile = -> Sketch021
  ReferenceAxis = -> Sketch021 [N_Axis]
  Reversed = true
  Suppressed = false
  Type = 4
FEATURE [PartDesign::Pad] Pad013
  BaseFeature = -> Pad012
  Direction = (0,0,1)
  Length = 37.5
  Length2 = -12.5
  Profile = -> Sketch022
  ReferenceAxis = -> Sketch022 [N_Axis]
  Suppressed = false
  Type = 4
FEATURE [Sketcher::SketchObject] Sketch_1
  ArcFitTolerance = 0
  FullyConstrained = false
  MakeInternals = false
  sketch-geometry (8):
    g0: Circle [constr] CenterX=0 CenterY=0 CenterZ=0 NormalX=0 NormalY=0 NormalZ=1 AngleXU=0 Radius=65.5
    g1: ArcOfCircle [constr] CenterX=0 CenterY=0 CenterZ=0 NormalX=0 NormalY=0 NormalZ=1 AngleXU=0 Radius=65.5 StartAngle=1.5708 EndAngle=4.71239
    g2: LineSegment StartX=145.598 StartY=65.5 StartZ=0 EndX=0 EndY=65.5 EndZ=0
    g3: LineSegment StartX=145.598 StartY=-65.5 StartZ=0 EndX=0 EndY=-65.5 EndZ=0
    g4: LineSegment StartX=145.598 StartY=65.5 StartZ=0 EndX=145.598 EndY=-65.5 EndZ=0
    g5: LineSegment StartX=-153.016 StartY=65.5 StartZ=0 EndX=0 EndY=65.5 EndZ=0
    g6: LineSegment StartX=-1.2e-14 StartY=-65.5 StartZ=0 EndX=-153.016 EndY=-65.5 EndZ=0
    g7: LineSegment StartX=-153.016 StartY=-65.5 StartZ=0 EndX=-153.016 EndY=65.5 EndZ=0
  constraints (18):
    c: Coincident(g0,g-1)
    c: Diameter(g0) = 131
    c: Coincident(g1,g0)
    c: PointOnObject(g1,g0)
    c: Horizontal(g2)
    c: Horizontal(g3)
    c: Tangent(g3,g1) = 1.5708
    c: Tangent(g1,g2) = -1.5708
    c: Coincident(g4,g2)
    c: Coincident(g4,g3)
    c: Vertical(g4)
    c: Coincident(g6,g7)
    c: Coincident(g7,g5)
    c: Horizontal(g5)
    c: Horizontal(g6)
    c: Vertical(g7)
    c: Coincident(g5,g2)
    c: Coincident(g6,g3)
FEATURE [PartDesign::Pocket] Pocket005
  BaseFeature = -> Pad013
  Direction = (0,0,-1)
  Length = 6.5
  Length2 = 13
  Profile = -> Sketch_1
  ReferenceAxis = -> Sketch_1 [N_Axis]
  Suppressed = false
  Type = 4
FEATURE [PartDesign::CoordinateSystem] Block_ribb
  AttacherType = Attacher::AttachEngine3D
  AttachmentSupport = -> [Pocket005]
  MapMode = 2
FEATURE [Sketcher::SketchObject] Sketch_2
  ArcFitTolerance = 0
  FullyConstrained = false
  MakeInternals = false
  sketch-geometry (44):
    g0: LineSegment StartX=-0.25 StartY=33.6074 StartZ=0 EndX=-0.25 EndY=47.5 EndZ=0
    g1: LineSegment StartX=-0.25 StartY=47.5 StartZ=0 EndX=126.736 EndY=47.5 EndZ=0
    g2: LineSegment StartX=126.736 StartY=47.5 StartZ=0 EndX=126.736 EndY=47 EndZ=0
    g3: LineSegment StartX=126.736 StartY=47 StartZ=0 EndX=0.25 EndY=47 EndZ=0
    g4: LineSegment StartX=0.25 StartY=47 StartZ=0 EndX=0.25 EndY=33.6074 EndZ=0
    g5: LineSegment StartX=0.25 StartY=33.6074 StartZ=0 EndX=-0.25 EndY=33.6074 EndZ=0
    g6: ArcOfCircle CenterX=86.75 CenterY=76.5 CenterZ=0 NormalX=0 NormalY=0 NormalZ=1 AngleXU=0 Radius=1.5 StartAngle=4.71239 EndAngle=6.28319
    g7: ArcOfCircle CenterX=8.25 CenterY=76.5 CenterZ=0 NormalX=0 NormalY=0 NormalZ=1 AngleXU=0 Radius=1.5 StartAngle=3.14159 EndAngle=4.71239
    g8: LineSegment StartX=86.75 StartY=75 StartZ=0 EndX=8.25 EndY=75 EndZ=0
    g9: LineSegment StartX=88.25 StartY=105 StartZ=0 EndX=6.75 EndY=105 EndZ=0
    g10: LineSegment StartX=6.75 StartY=105 StartZ=0 EndX=6.75 EndY=76.5 EndZ=0
    g11: LineSegment StartX=88.25 StartY=105 StartZ=0 EndX=88.25 EndY=76.5 EndZ=0
    g12: GeomPoint [constr] X=47.5 Y=105 Z=0
    g13: Circle CenterX=-118 CenterY=93 CenterZ=0 NormalX=0 NormalY=0 NormalZ=1 AngleXU=0 Radius=6
    g14: Circle CenterX=118 CenterY=93 CenterZ=0 NormalX=0 NormalY=0 NormalZ=1 AngleXU=0 Radius=6
    g15: LineSegment StartX=-0.067348 StartY=-33.6074 StartZ=0 EndX=-0.067348 EndY=-47.5 EndZ=0
    g16: LineSegment StartX=-0.067348 StartY=-47.5 StartZ=0 EndX=126.736 EndY=-47.5 EndZ=0
    g17: LineSegment StartX=126.736 StartY=-47.5 StartZ=0 EndX=126.736 EndY=-47 EndZ=0
    g18: LineSegment StartX=126.736 StartY=-47 StartZ=0 EndX=0.25 EndY=-47 EndZ=0
    g19: LineSegment StartX=0.25 StartY=-47 StartZ=0 EndX=0.25 EndY=-33.6074 EndZ=0
    g20: LineSegment StartX=0.25 StartY=-33.6074 StartZ=0 EndX=-0.067348 EndY=-33.6074 EndZ=0
    g21: ArcOfCircle CenterX=-86.75 CenterY=76.5 CenterZ=0 NormalX=0 NormalY=0 NormalZ=1 AngleXU=0 Radius=1.5 StartAngle=3.14159 EndAngle=4.71239
    g22: ArcOfCircle CenterX=-8.25 CenterY=76.5 CenterZ=0 NormalX=0 NormalY=0 NormalZ=1 AngleXU=0 Radius=1.5 StartAngle=4.71239 EndAngle=6.28319
    g23: LineSegment StartX=-86.75 StartY=75 StartZ=0 EndX=-8.25 EndY=75 EndZ=0
    g24: LineSegment StartX=-88.25 StartY=105 StartZ=0 EndX=-6.75 EndY=105 EndZ=0
    g25: LineSegment StartX=-6.75 StartY=105 StartZ=0 EndX=-6.75 EndY=76.5 EndZ=0
    g26: LineSegment StartX=-88.25 StartY=105 StartZ=0 EndX=-88.25 EndY=76.5 EndZ=0
    g27: GeomPoint [constr] X=-47.5 Y=105 Z=0
    g28: ArcOfCircle CenterX=86.75 CenterY=-76.5 CenterZ=0 NormalX=0 NormalY=0 NormalZ=1 AngleXU=0 Radius=1.5 StartAngle=0 EndAngle=1.5708
    g29: ArcOfCircle CenterX=8.25 CenterY=-76.5 CenterZ=0 NormalX=0 NormalY=0 NormalZ=1 AngleXU=0 Radius=1.5 StartAngle=1.5708 EndAngle=3.14159
    g30: LineSegment StartX=86.75 StartY=-75 StartZ=0 EndX=8.25 EndY=-75 EndZ=0
    g31: LineSegment StartX=88.25 StartY=-105 StartZ=0 EndX=6.75 EndY=-105 EndZ=0
    g32: LineSegment StartX=6.75 StartY=-105 StartZ=0 EndX=6.75 EndY=-76.5 EndZ=0
    g33: LineSegment StartX=88.25 StartY=-105 StartZ=0 EndX=88.25 EndY=-76.5 EndZ=0
    g34: GeomPoint [constr] X=47.5 Y=-105 Z=0
    g35: Circle CenterX=-118 CenterY=-93 CenterZ=0 NormalX=0 NormalY=0 NormalZ=1 AngleXU=0 Radius=6
    g36: Circle CenterX=118 CenterY=-93 CenterZ=0 NormalX=0 NormalY=0 NormalZ=1 AngleXU=0 Radius=6
    g37: ArcOfCircle CenterX=-86.75 CenterY=-76.5 CenterZ=0 NormalX=0 NormalY=0 NormalZ=1 AngleXU=0 Radius=1.5 StartAngle=1.5708 EndAngle=3.14159
    g38: ArcOfCircle CenterX=-8.25 CenterY=-76.5 CenterZ=0 NormalX=0 NormalY=0 NormalZ=1 AngleXU=0 Radius=1.5 StartAngle=0 EndAngle=1.5708
    g39: LineSegment StartX=-86.75 StartY=-75 StartZ=0 EndX=-8.25 EndY=-75 EndZ=0
    g40: LineSegment StartX=-88.25 StartY=-105 StartZ=0 EndX=-6.75 EndY=-105 EndZ=0
    g41: LineSegment StartX=-6.75 StartY=-105 StartZ=0 EndX=-6.75 EndY=-76.5 EndZ=0
    g42: LineSegment StartX=-88.25 StartY=-105 StartZ=0 EndX=-88.25 EndY=-76.5 EndZ=0
    g43: GeomPoint [constr] X=-47.5 Y=-105 Z=0
  constraints (95):
    c: Vertical(g0)
    c: Coincident(g0,g1)
    c: Horizontal(g1)
    c: Coincident(g1,g2)
    c: Coincident(g2,g3)
    c: Horizontal(g3)
    c: Coincident(g3,g4)
    c: Vertical(g4)
    c: Coincident(g4,g5)
    c: Coincident(g5,g0)
    c: Vertical(g2)
    c: DistanceY(g2,g2) = 0.5
    c: DistanceX(g5,g5) = 0.5
    c: Tangent(g6,g8) = 1.5708
    c: Tangent(g8,g7) = 1.5708
    c: Equal(g6,g7)
    c: Horizontal(g8)
    c: Horizontal(g9)
    c: Vertical(g11)
    c: Vertical(g10)
    c: Tangent(g6,g11) = 1.5708
    c: Tangent(g7,g10) = -1.5708
    c: Coincident(g11,g9)
    c: Coincident(g9,g10)
    c: Symmetric(g9,g9,g12)
    c: Radius(g7) = 1.5
    c: Distance(g7,g9) = 30
    c: Diameter(g13) = 12
    c: Symmetric(g0,g4,g-2)
    c: DistanceY(g-1,g13) = 93
    c: DistanceX(g13,g-1) = 118
    c: DistanceY(g-1,g9) = 105
    c: DistanceX(g9,g9) = 81.5
    c: DistanceX(g-1,g9) = 6.75
    c: Diameter(g14) = 12
    c: Vertical(g15)
    c: Coincident(g15,g16)
    c: Horizontal(g16)
    c: Coincident(g16,g17)
    c: Coincident(g17,g18)
    c: Horizontal(g18)
    c: Coincident(g18,g19)
    c: Vertical(g19)
    c: Coincident(g19,g20)
    c: Coincident(g20,g15)
    c: Vertical(g17)
    c: Tangent(g21,g23) = -1.5708
    c: Tangent(g23,g22) = -1.5708
    c: Equal(g21,g22)
    c: Horizontal(g23)
    c: Horizontal(g24)
    c: Vertical(g26)
    c: Vertical(g25)
    c: Tangent(g21,g26) = -1.5708
    c: Tangent(g22,g25) = 1.5708
    c: Coincident(g26,g24)
    c: Coincident(g24,g25)
    c: Symmetric(g24,g24,g27)
    c: Radius(g22) = 1.5
    c: Distance(g22,g24) = 30
    c: Tangent(g28,g30) = -1.5708
    c: Tangent(g30,g29) = -1.5708
    c: Equal(g28,g29)
    c: Horizontal(g30)
    c: Horizontal(g31)
    c: Vertical(g33)
    c: Vertical(g32)
    c: Tangent(g28,g33) = -1.5708
    c: Tangent(g29,g32) = 1.5708
    c: Coincident(g33,g31)
    c: Coincident(g31,g32)
    c: Symmetric(g31,g31,g34)
    c: Radius(g29) = 1.5
    c: Distance(g29,g31) = 30
    c: Diameter(g35) = 12
    c: Diameter(g36) = 12
    c: Tangent(g37,g39) = 1.5708
    c: Tangent(g39,g38) = 1.5708
    c: Equal(g37,g38)
    c: Horizontal(g39)
    c: Horizontal(g40)
    c: Vertical(g42)
    c: Vertical(g41)
    c: Tangent(g37,g42) = 1.5708
    c: Tangent(g38,g41) = -1.5708
    c: Coincident(g42,g40)
    c: Coincident(g40,g41)
    c: Symmetric(g40,g40,g43)
    c: Radius(g38) = 1.5
    c: Distance(g38,g40) = 30
    c: Symmetric(g19,g4,g-1)
    c: Horizontal(g20)
    c: Symmetric(g17,g2,g-1)
    c: DistanceY(g17,g17) = 0.5
    c: DistanceY(g16,g1) = 95
FEATURE [PartDesign::Pocket] Pocket006
  BaseFeature = -> Pocket005
  Direction = (0,0,-1)
  Length = 50
  Length2 = 50
  Profile = -> Sketch_2
  ReferenceAxis = -> Sketch_2 [N_Axis]
  Suppressed = false
  Type = 4
FEATURE [Sketcher::SketchObject] Sketch028
  ArcFitTolerance = 0
  FullyConstrained = true
  MakeInternals = false
  MapMode = 5
  Placement = pos=(0,-75,0) rot=(1,0,0;1.5708rad)
  sketch-geometry (1):
    g0: Circle CenterX=74 CenterY=-21.75 CenterZ=0 NormalX=0 NormalY=0 NormalZ=1 AngleXU=0 Radius=6
  constraints (3):
    c: Diameter(g0) = 12
    c: DistanceY(g0,g-1) = 21.75
    c: DistanceX(g-1,g0) = 74
FEATURE [PartDesign::Pocket] Pocket011
  BaseFeature = -> Pocket006
  Direction = (0,1,-2e-16)
  Length = 5
  Length2 = 5
  Profile = -> Sketch028
  ReferenceAxis = -> Sketch028 [N_Axis]
  Suppressed = false
  Type = 1
FEATURE [PartDesign::Body] Body061  label="перегородка"
  AllowCompound = false
  Group = -> [Sketch022,Sketch021,Pad012,Pad013,Sketch_1,Pocket005,Block_ribb,Sketch_2,Pocket006,Sketch028,Pocket011]
  Origin = -> Origin062
  Tip = -> Pocket011
COMPONENT P12 — recipe-attached ("Перегородка_передняя", modeled in this document).
Construction recipe (the document's own serialized feature program — sketch geometry with constraints, then the solid features built on it; lengths are millimeters unless a unit is written):

FEATURE [PartDesign::Pad] Pad017
  Direction = (0,0,1)
  Length = 37
  Length2 = 22.5
  Profile = -> Sketch021
  ReferenceAxis = -> Sketch021 [N_Axis]
  Reversed = true
  Suppressed = false
  Type = 4
FEATURE [PartDesign::Pocket] Pocket017
  BaseFeature = -> Pad017
  Direction = (0,0,-1)
  Length = 8.5
  Length2 = 13
  Profile = -> Sketch_1
  ReferenceAxis = -> Sketch_1 [N_Axis]
  Suppressed = false
  Type = 4
FEATURE [PartDesign::CoordinateSystem] Block_ribb001
  AttacherType = Attacher::AttachEngine3D
  AttachmentSupport = -> [Pocket017]
  MapMode = 2
FEATURE [PartDesign::Pocket] Pocket018
  BaseFeature = -> Pocket017
  Direction = (0,0,-1)
  Length = 50
  Length2 = 50
  Profile = -> Sketch_2
  ReferenceAxis = -> Sketch_2 [N_Axis]
  Suppressed = false
  Type = 4
FEATURE [PartDesign::Pocket] Pocket019
  BaseFeature = -> Pocket018
  Direction = (0,1,-2e-16)
  Length = 5
  Length2 = 5
  Profile = -> Sketch028
  ReferenceAxis = -> Sketch028 [N_Axis]
  Suppressed = false
  Type = 1
FEATURE [Sketcher::SketchObject] Sketch034
  ArcFitTolerance = 0
  AttachmentSupport = -> [XY_Plane062]
  FullyConstrained = false
  MakeInternals = false
  MapMode = 5
  sketch-geometry (4):
    g0: LineSegment StartX=-154.224 StartY=65.5 StartZ=0 EndX=161.628 EndY=65.5 EndZ=0
    g1: LineSegment StartX=161.628 StartY=65.5 StartZ=0 EndX=161.628 EndY=-65.5 EndZ=0
    g2: LineSegment StartX=161.628 StartY=-65.5 StartZ=0 EndX=-154.224 EndY=-65.5 EndZ=0
    g3: LineSegment StartX=-154.224 StartY=-65.5 StartZ=0 EndX=-154.224 EndY=65.5 EndZ=0
  constraints (9):
    c: Coincident(g0,g1)
    c: Coincident(g1,g2)
    c: Coincident(g2,g3)
    c: Coincident(g3,g0)
    c: Horizontal(g0)
    c: Horizontal(g2)
    c: Vertical(g3)
    c: Symmetric(g1,g0,g-1)
    c: DistanceY(g1,g1) = 131
FEATURE [PartDesign::Pocket] Pocket020
  BaseFeature = -> Pocket019
  Direction = (0,0,-1)
  Length = 25
  Length2 = -10.5
  Profile = -> Sketch034
  ReferenceAxis = -> Sketch034 [N_Axis]
  Reversed = true
  Suppressed = false
  Type = 4
FEATURE [PartDesign::Body] Body063  label="Перегородка_передняя"
  AllowCompound = false
  Group = -> [Pad017,Pocket017,Block_ribb001,Pocket018,Pocket019,Sketch034,Pocket020]
  Origin = -> Origin064
  Tip = -> Pocket020
COMPONENT P13 — recipe-attached ("перегородка_ползуна", modeled in this document).
Construction recipe (the document's own serialized feature program — sketch geometry with constraints, then the solid features built on it; lengths are millimeters unless a unit is written):

FEATURE [PartDesign::CoordinateSystem] Block_ribb002
  AttacherType = Attacher::AttachEngine3D
  MapMode = 2
FEATURE [PartDesign::Pad] Pad018
  Direction = (0,0,1)
  Length = 12.5
  Length2 = 12.5
  Profile = -> Sketch021
  ReferenceAxis = -> Sketch021 [N_Axis]
  Reversed = true
  Suppressed = false
  Type = 4
FEATURE [Sketcher::SketchObject] Sketch035
  ArcFitTolerance = 0
  FullyConstrained = false
  MakeInternals = false
  MapMode = 5
  sketch-geometry (9):
    g0: LineSegment [constr] StartX=-110 StartY=-105 StartZ=0 EndX=-65.5 EndY=-105 EndZ=0
    g1: LineSegment [constr] StartX=-65.5 StartY=-105 StartZ=0 EndX=-65.5 EndY=105 EndZ=0
    g2: LineSegment [constr] StartX=-65.5 StartY=105 StartZ=0 EndX=-110 EndY=105 EndZ=0
    g3: LineSegment [constr] StartX=-110 StartY=105 StartZ=0 EndX=-110 EndY=-105 EndZ=0
    g4: LineSegment [constr] StartX=65.5 StartY=52.7372 StartZ=0 EndX=65.5 EndY=105 EndZ=0
    g5: LineSegment StartX=-110 StartY=-105 StartZ=0 EndX=65.5 EndY=-105 EndZ=0
    g6: LineSegment StartX=65.5 StartY=-105 StartZ=0 EndX=65.5 EndY=105 EndZ=0
    g7: LineSegment StartX=65.5 StartY=105 StartZ=0 EndX=-110 EndY=105 EndZ=0
    g8: LineSegment StartX=-110 StartY=105 StartZ=0 EndX=-110 EndY=-105 EndZ=0
  constraints (23):
    c: Coincident(g0,g1)
    c: Coincident(g1,g2)
    c: Coincident(g2,g3)
    c: Coincident(g3,g0)
    c: Horizontal(g0)
    c: Horizontal(g2)
    c: Vertical(g3)
    c: Vertical(g4)
    c: DistanceX(g1,g4) = 131
    c: Symmetric(g1,g4,g-2)
    c: DistanceY(g1,g1) = 210
    c: DistanceX(g0,g0) = 44.5
    c: Symmetric(g0,g1,g-1)
    c: Coincident(g5,g6)
    c: Coincident(g6,g7)
    c: Coincident(g7,g8)
    c: Coincident(g8,g5)
    c: Horizontal(g5)
    c: Horizontal(g7)
    c: Vertical(g6)
    c: Vertical(g8)
    c: Coincident(g5,g0)
    c: Coincident(g6,g4)
FEATURE [Sketcher::SketchObject] Sketch_004
  ArcFitTolerance = 0
  FullyConstrained = false
  MakeInternals = false
  sketch-geometry (32):
    g0: ArcOfCircle CenterX=86.75 CenterY=76.5 CenterZ=0 NormalX=0 NormalY=0 NormalZ=1 AngleXU=0 Radius=1.5 StartAngle=4.71239 EndAngle=6.28319
    g1: ArcOfCircle CenterX=8.25 CenterY=76.5 CenterZ=0 NormalX=0 NormalY=0 NormalZ=1 AngleXU=0 Radius=1.5 StartAngle=3.14159 EndAngle=4.71239
    g2: LineSegment StartX=86.75 StartY=75 StartZ=0 EndX=8.25 EndY=75 EndZ=0
    g3: LineSegment StartX=88.25 StartY=105 StartZ=0 EndX=6.75 EndY=105 EndZ=0
    g4: LineSegment StartX=6.75 StartY=105 StartZ=0 EndX=6.75 EndY=76.5 EndZ=0
    g5: LineSegment StartX=88.25 StartY=105 StartZ=0 EndX=88.25 EndY=76.5 EndZ=0
    g6: GeomPoint [constr] X=47.5 Y=105 Z=0
    g7: Circle CenterX=-118 CenterY=93 CenterZ=0 NormalX=0 NormalY=0 NormalZ=1 AngleXU=0 Radius=6
    g8: Circle CenterX=118 CenterY=93 CenterZ=0 NormalX=0 NormalY=0 NormalZ=1 AngleXU=0 Radius=6
    g9: ArcOfCircle CenterX=-86.75 CenterY=76.5 CenterZ=0 NormalX=0 NormalY=0 NormalZ=1 AngleXU=0 Radius=1.5 StartAngle=3.14159 EndAngle=4.71239
    g10: ArcOfCircle CenterX=-8.25 CenterY=76.5 CenterZ=0 NormalX=0 NormalY=0 NormalZ=1 AngleXU=0 Radius=1.5 StartAngle=4.71239 EndAngle=6.28319
    g11: LineSegment StartX=-86.75 StartY=75 StartZ=0 EndX=-8.25 EndY=75 EndZ=0
    g12: LineSegment StartX=-88.25 StartY=105 StartZ=0 EndX=-6.75 EndY=105 EndZ=0
    g13: LineSegment StartX=-6.75 StartY=105 StartZ=0 EndX=-6.75 EndY=76.5 EndZ=0
    g14: LineSegment StartX=-88.25 StartY=105 StartZ=0 EndX=-88.25 EndY=76.5 EndZ=0
    g15: GeomPoint [constr] X=-47.5 Y=105 Z=0
    g16: ArcOfCircle CenterX=86.75 CenterY=-76.5 CenterZ=0 NormalX=0 NormalY=0 NormalZ=1 AngleXU=0 Radius=1.5 StartAngle=0 EndAngle=1.5708
    g17: ArcOfCircle CenterX=8.25 CenterY=-76.5 CenterZ=0 NormalX=0 NormalY=0 NormalZ=1 AngleXU=0 Radius=1.5 StartAngle=1.5708 EndAngle=3.14159
    g18: LineSegment StartX=86.75 StartY=-75 StartZ=0 EndX=8.25 EndY=-75 EndZ=0
    g19: LineSegment StartX=88.25 StartY=-105 StartZ=0 EndX=6.75 EndY=-105 EndZ=0
    g20: LineSegment StartX=6.75 StartY=-105 StartZ=0 EndX=6.75 EndY=-76.5 EndZ=0
    g21: LineSegment StartX=88.25 StartY=-105 StartZ=0 EndX=88.25 EndY=-76.5 EndZ=0
    g22: GeomPoint [constr] X=47.5 Y=-105 Z=0
    g23: Circle CenterX=-118 CenterY=-93 CenterZ=0 NormalX=0 NormalY=0 NormalZ=1 AngleXU=0 Radius=6
    g24: Circle CenterX=118 CenterY=-93 CenterZ=0 NormalX=0 NormalY=0 NormalZ=1 AngleXU=0 Radius=6
    g25: ArcOfCircle CenterX=-86.75 CenterY=-76.5 CenterZ=0 NormalX=0 NormalY=0 NormalZ=1 AngleXU=0 Radius=1.5 StartAngle=1.5708 EndAngle=3.14159
    g26: ArcOfCircle CenterX=-8.25 CenterY=-76.5 CenterZ=0 NormalX=0 NormalY=0 NormalZ=1 AngleXU=0 Radius=1.5 StartAngle=0 EndAngle=1.5708
    g27: LineSegment StartX=-86.75 StartY=-75 StartZ=0 EndX=-8.25 EndY=-75 EndZ=0
    g28: LineSegment StartX=-88.25 StartY=-105 StartZ=0 EndX=-6.75 EndY=-105 EndZ=0
    g29: LineSegment StartX=-6.75 StartY=-105 StartZ=0 EndX=-6.75 EndY=-76.5 EndZ=0
    g30: LineSegment StartX=-88.25 StartY=-105 StartZ=0 EndX=-88.25 EndY=-76.5 EndZ=0
    g31: GeomPoint [constr] X=-47.5 Y=-105 Z=0
  constraints (65):
    c: Tangent(g0,g2) = 1.5708
    c: Tangent(g2,g1) = 1.5708
    c: Equal(g0,g1)
    c: Horizontal(g2)
    c: Horizontal(g3)
    c: Vertical(g5)
    c: Vertical(g4)
    c: Tangent(g0,g5) = 1.5708
    c: Tangent(g1,g4) = -1.5708
    c: Coincident(g5,g3)
    c: Coincident(g3,g4)
    c: Symmetric(g3,g3,g6)
    c: Radius(g1) = 1.5
    c: Distance(g1,g3) = 30
    c: Diameter(g7) = 12
    c: DistanceY(g-1,g7) = 93
    c: DistanceX(g7,g-1) = 118
    c: DistanceY(g-1,g3) = 105
    c: DistanceX(g3,g3) = 81.5
    c: DistanceX(g-1,g3) = 6.75
    c: Diameter(g8) = 12
    c: Tangent(g9,g11) = -1.5708
    c: Tangent(g11,g10) = -1.5708
    c: Equal(g9,g10)
    c: Horizontal(g11)
    c: Horizontal(g12)
    c: Vertical(g14)
    c: Vertical(g13)
    c: Tangent(g9,g14) = -1.5708
    c: Tangent(g10,g13) = 1.5708
    c: Coincident(g14,g12)
    c: Coincident(g12,g13)
    c: Symmetric(g12,g12,g15)
    c: Radius(g10) = 1.5
    c: Distance(g10,g12) = 30
    c: Tangent(g16,g18) = -1.5708
    c: Tangent(g18,g17) = -1.5708
    c: Equal(g16,g17)
    c: Horizontal(g18)
    c: Horizontal(g19)
    c: Vertical(g21)
    c: Vertical(g20)
    c: Tangent(g16,g21) = -1.5708
    c: Tangent(g17,g20) = 1.5708
    c: Coincident(g21,g19)
    c: Coincident(g19,g20)
    c: Symmetric(g19,g19,g22)
    c: Radius(g17) = 1.5
    c: Distance(g17,g19) = 30
    c: Diameter(g23) = 12
    c: Diameter(g24) = 12
    c: Tangent(g25,g27) = 1.5708
    c: Tangent(g27,g26) = 1.5708
    c: Equal(g25,g26)
    c: Horizontal(g27)
    c: Horizontal(g28)
    c: Vertical(g30)
    c: Vertical(g29)
    c: Tangent(g25,g30) = 1.5708
    c: Tangent(g26,g29) = -1.5708
    c: Coincident(g30,g28)
    c: Coincident(g28,g29)
    c: Symmetric(g28,g28,g31)
    c: Radius(g26) = 1.5
    c: Distance(g26,g28) = 30
FEATURE [PartDesign::Pocket] Pocket021
  BaseFeature = -> Pad018
  Direction = (0,0,-1)
  Length = 20
  Length2 = 20
  Profile = -> Sketch_004
  ReferenceAxis = -> Sketch_004 [N_Axis]
  Suppressed = false
  Type = 4
FEATURE [PartDesign::Pocket] Pocket022
  BaseFeature = -> Pocket021
  Direction = (0,0,-1)
  Length = 20
  Length2 = 20
  Profile = -> Sketch035
  ReferenceAxis = -> Sketch035 [N_Axis]
  Suppressed = false
  Type = 4
FEATURE [PartDesign::Body] Body064  label="перегородка_ползуна"
  AllowCompound = false
  Group = -> [Sketch035,Pad018,Block_ribb002,Sketch_004,Pocket021,Pocket022]
  Origin = -> Origin065
  Tip = -> Pocket022
COMPONENT P14 — recipe-attached ("направляющая_орто_ползуна", modeled in this document).
Construction recipe (the document's own serialized feature program — sketch geometry with constraints, then the solid features built on it; lengths are millimeters unless a unit is written):

FEATURE [Sketcher::SketchObject] Sketch038
  ArcFitTolerance = 0
  FullyConstrained = true
  MakeInternals = false
  MapMode = 5
  sketch-geometry (26):
    g0: LineSegment [constr] StartX=-103 StartY=-65 StartZ=0 EndX=103 EndY=-65 EndZ=0
    g1: LineSegment StartX=103 StartY=-65 StartZ=0 EndX=103 EndY=65 EndZ=0
    g2: LineSegment [constr] StartX=103 StartY=65 StartZ=0 EndX=-103 EndY=65 EndZ=0
    g3: LineSegment StartX=-103 StartY=65 StartZ=0 EndX=-103 EndY=-65 EndZ=0
    g4: ArcOfCircle CenterX=0 CenterY=40 CenterZ=0 NormalX=0 NormalY=0 NormalZ=1 AngleXU=0 Radius=20.25 StartAngle=1.05267 EndAngle=2.08892
    g5: ArcOfCircle CenterX=0 CenterY=0 CenterZ=0 NormalX=0 NormalY=0 NormalZ=1 AngleXU=0 Radius=55 StartAngle=2.08892 EndAngle=4.19427
    g6: ArcOfCircle CenterX=0 CenterY=0 CenterZ=0 NormalX=0 NormalY=0 NormalZ=1 AngleXU=0 Radius=55 StartAngle=5.23051 EndAngle=7.33586
    g7: ArcOfCircle CenterX=0 CenterY=-40 CenterZ=0 NormalX=0 NormalY=0 NormalZ=1 AngleXU=0 Radius=20.25 StartAngle=4.19427 EndAngle=5.23051
    g8: LineSegment StartX=-27.2388 StartY=47.7813 StartZ=0 EndX=-10.0288 EndY=57.5922 EndZ=0
    g9: LineSegment StartX=10.0288 StartY=57.5922 StartZ=0 EndX=27.2388 EndY=47.7813 EndZ=0
    g10: LineSegment StartX=-27.2388 StartY=-47.7812 StartZ=0 EndX=-10.0288 EndY=-57.5922 EndZ=0
    g11: LineSegment StartX=10.0288 StartY=-57.5922 StartZ=0 EndX=27.2388 EndY=-47.7812 EndZ=0
    g12: LineSegment StartX=-99 StartY=69.5 StartZ=0 EndX=99 EndY=69.5 EndZ=0
    g13: LineSegment StartX=-103 StartY=65 StartZ=0 EndX=-103 EndY=65.5 EndZ=0
    g14: LineSegment StartX=103 StartY=65.5 StartZ=0 EndX=103 EndY=65 EndZ=0
    g15: ArcOfCircle CenterX=-99 CenterY=65.5 CenterZ=0 NormalX=0 NormalY=0 NormalZ=1 AngleXU=0 Radius=4 StartAngle=1.5708 EndAngle=3.14159
    g16: ArcOfCircle CenterX=99 CenterY=65.5 CenterZ=0 NormalX=0 NormalY=0 NormalZ=1 AngleXU=0 Radius=4 StartAngle=4e-16 EndAngle=1.5708
    g17: ArcOfCircle CenterX=-99 CenterY=-65.5 CenterZ=0 NormalX=0 NormalY=0 NormalZ=1 AngleXU=0 Radius=4 StartAngle=3.14159 EndAngle=4.71239
    g18: LineSegment StartX=-103 StartY=-65 StartZ=0 EndX=-103 EndY=-65.5 EndZ=0
    g19: LineSegment StartX=-99 StartY=-69.5 StartZ=0 EndX=99 EndY=-69.5 EndZ=0
    g20: ArcOfCircle CenterX=99 CenterY=-65.5 CenterZ=0 NormalX=0 NormalY=0 NormalZ=1 AngleXU=0 Radius=4 StartAngle=4.71239 EndAngle=6.28319
    g21: LineSegment StartX=103 StartY=-65.5 StartZ=0 EndX=103 EndY=-65 EndZ=0
    g22: Circle CenterX=-95 CenterY=55 CenterZ=0 NormalX=0 NormalY=0 NormalZ=1 AngleXU=0 Radius=3
    g23: Circle CenterX=95 CenterY=55 CenterZ=0 NormalX=0 NormalY=0 NormalZ=1 AngleXU=0 Radius=3
    g24: Circle CenterX=-95 CenterY=-55 CenterZ=0 NormalX=0 NormalY=0 NormalZ=1 AngleXU=0 Radius=3
    g25: Circle CenterX=95 CenterY=-55 CenterZ=0 NormalX=0 NormalY=0 NormalZ=1 AngleXU=0 Radius=3
  constraints (58):
    c: Coincident(g0,g1)
    c: Coincident(g1,g2)
    c: Coincident(g2,g3)
    c: Coincident(g3,g0)
    c: Horizontal(g0)
    c: Vertical(g1)
    c: Symmetric(g2,g1,g-2)
    c: Symmetric(g2,g0,g-1)
    c: DistanceX(g2,g2) = 206
    c: PointOnObject(g4,g-2)
    c: Diameter(g4) = 40.5
    c: Equal(g4,g7)
    c: Symmetric(g4,g7,g-1)
    c: Equal(g5,g6)
    c: Tangent(g5,g10) = -1.5708
    c: Tangent(g5,g8) = 1.5708
    c: Tangent(g4,g8) = 1.5708
    c: Tangent(g4,g9) = 1.5708
    c: Tangent(g7,g11) = -1.5708
    c: Tangent(g7,g10) = -1.5708
    c: Tangent(g6,g9) = 1.5708
    c: Tangent(g6,g11) = -1.5708
    c: Distance(g-1,g4) = 40
    c: DistanceY(g1,g1) = 130
    c: Radius(g6) = 55
    c: Coincident(g5,g-1)
    c: Coincident(g6,g5)
    c: Coincident(g13,g3)
    c: Coincident(g14,g1)
    c: Tangent(g13,g15) = 1.5708
    c: Tangent(g12,g15) = 1.5708
    c: Tangent(g12,g16) = 1.5708
    c: Tangent(g14,g16) = 1.5708
    c: Vertical(g13)
    c: Vertical(g14)
    c: Symmetric(g15,g16,g-2)
    c: DistanceY(g1,g12) = 4.5
    c: Radius(g16) = 4
    c: Tangent(g18,g17) = -1.5708
    c: Tangent(g19,g17) = -1.5708
    c: Tangent(g19,g20) = -1.5708
    c: Vertical(g18)
    c: Symmetric(g17,g20,g-2)
    c: Symmetric(g17,g15,g-1)
    c: Coincident(g18,g3)
    c: Coincident(g21,g1)
    c: Vertical(g21)
    c: Equal(g21,g18)
    c: Coincident(g20,g21)
    c: Equal(g22,g23)
    c: Equal(g23,g25)
    c: Equal(g25,g24)
    c: Diameter(g23) = 6
    c: Symmetric(g22,g23,g-2)
    c: Symmetric(g24,g25,g-2)
    c: Symmetric(g24,g22,g-1)
    c: DistanceY(g24,g22) = 110
    c: DistanceX(g24,g25) = 190
FEATURE [PartDesign::Pad] Pad020
  Direction = (0,0,1)
  Length = 22.5
  Length2 = 5.5
  Midplane = true
  Profile = -> Sketch038
  ReferenceAxis = -> Sketch038 [N_Axis]
  Suppressed = false
  Type = 4
FEATURE [PartDesign::CoordinateSystem] Shtok003
  AttacherType = Attacher::AttachEngine3D
  AttachmentSupport = -> [Sketch038]
  MapMode = 2
FEATURE [Sketcher::SketchObject] Sketch061
  ArcFitTolerance = 0
  AttachmentSupport = -> [Pad020]
  FullyConstrained = false
  MakeInternals = false
  MapMode = 5
  Placement = pos=(0,0,22.5) rot=(0,0,1;0rad)
  sketch-geometry (5):
    g0: Circle CenterX=0 CenterY=0 CenterZ=0 NormalX=0 NormalY=0 NormalZ=1 AngleXU=0 Radius=8.25
    g1: LineSegment StartX=-79.3827 StartY=20 StartZ=0 EndX=79.3827 EndY=20 EndZ=0
    g2: LineSegment StartX=79.3827 StartY=20 StartZ=0 EndX=79.3827 EndY=-20 EndZ=0
    g3: LineSegment StartX=79.3827 StartY=-20 StartZ=0 EndX=-79.3827 EndY=-20 EndZ=0
    g4: LineSegment StartX=-79.3827 StartY=-20 StartZ=0 EndX=-79.3827 EndY=20 EndZ=0
  constraints (12):
    c: Coincident(g0,g-1)
    c: Diameter(g0) = 16.5
    c: Coincident(g1,g2)
    c: Coincident(g2,g3)
    c: Coincident(g3,g4)
    c: Coincident(g4,g1)
    c: Horizontal(g1)
    c: Horizontal(g3)
    c: Vertical(g2)
    c: Vertical(g4)
    c: Symmetric(g3,g1,g0)
    c: DistanceY(g2,g2) = 40
FEATURE [PartDesign::Pad] Pad032
  BaseFeature = -> Pad020
  Direction = (0,0,1)
  Length = 16
  Length2 = 10
  Profile = -> Sketch061
  ReferenceAxis = -> Sketch061 [N_Axis]
  Reversed = true
  Suppressed = false
  Type = 0
FEATURE [PartDesign::Body] Body066  label="направляющая_орто_ползуна"
  AllowCompound = false
  Group = -> [Sketch038,Pad020,Shtok003,Sketch061,Pad032]
  Origin = -> Origin067
  Tip = -> Pad032
COMPONENT P15 — recipe-attached ("Поршень003", modeled in this document).
Construction recipe (the document's own serialized feature program — sketch geometry with constraints, then the solid features built on it; lengths are millimeters unless a unit is written):

FEATURE [Sketcher::SketchObject] Sketch041
  ArcFitTolerance = 0
  AttachmentSupport = -> [XY_Plane069]
  FullyConstrained = true
  MakeInternals = false
  MapMode = 5
  sketch-geometry (6):
    g0: Circle [constr] CenterX=0 CenterY=85 CenterZ=0 NormalX=0 NormalY=0 NormalZ=1 AngleXU=0 Radius=11.5
    g1: LineSegment StartX=-45.5 StartY=147 StartZ=0 EndX=45.5 EndY=147 EndZ=0
    g2: LineSegment StartX=-45.5 StartY=147 StartZ=0 EndX=-45.5 EndY=51 EndZ=0
    g3: LineSegment StartX=0 StartY=51 StartZ=0 EndX=-45.5 EndY=51 EndZ=0
    g4: LineSegment StartX=45.5 StartY=147 StartZ=0 EndX=45.5 EndY=51 EndZ=0
    g5: LineSegment StartX=0 StartY=51 StartZ=0 EndX=45.5 EndY=51 EndZ=0
  constraints (15):
    c: Coincident(g2,g1)
    c: Vertical(g2)
    c: Symmetric(g1,g1,g-2)
    c: DistanceX(g1,g1) = 91
    c: PointOnObject(g3,g-2)
    c: Vertical(g4)
    c: Block(g0)
    c: Coincident(g1,g4)
    c: DistanceY(g0,g1) = 62
    c: DistanceY(g3,g0) = 34
    c: Horizontal(g3)
    c: Coincident(g2,g3)
    c: Coincident(g5,g3)
    c: Coincident(g5,g4)
    c: Horizontal(g5)
FEATURE [PartDesign::Pad] Pad021
  Direction = (0,0,1)
  Length = 100
  Length2 = 10
  Midplane = true
  Profile = -> Sketch041
  ReferenceAxis = -> Sketch041 [N_Axis]
  Suppressed = false
  Type = 0
FEATURE [PartDesign::Body] Body070  label="Поршень003"
  AllowCompound = false
  Group = -> [Sketch041,Pad021]
  Origin = -> Origin071
  Tip = -> Pad021
COMPONENT P16 — recipe-attached ("Поршень_2T_92mm", modeled in this document).
Construction recipe (the document's own serialized feature program — sketch geometry with constraints, then the solid features built on it; lengths are millimeters unless a unit is written):

FEATURE [PartDesign::CoordinateSystem] Piston001
  AttacherType = Attacher::AttachEngine3D
  AttachmentSupport = -> [XZ_Plane071]
  MapMode = 2
  Placement = pos=(0,0,0) rot=(1,0,0;1.5708rad)
FEATURE [Sketcher::SketchObject] Sketch042
  ArcFitTolerance = 0
  AttachmentSupport = -> [XZ_Plane071]
  FullyConstrained = false
  MakeInternals = false
  MapMode = 5
  Placement = pos=(0,0,0) rot=(1,0,0;1.5708rad)
  sketch-geometry (2):
    g0: GeomPoint [constr] X=-87.5 Y=-1.47e-14 Z=0
    g1: Circle CenterX=0 CenterY=0 CenterZ=0 NormalX=0 NormalY=0 NormalZ=1 AngleXU=0 Radius=45.5
  constraints (2):
    c: Coincident(g1,g-1)
    c: Diameter(g1) = 91
FEATURE [PartDesign::Pad] Pad022
  Direction = (0,-1,2e-16)
  Length = 200
  Length2 = 10
  Placement = pos=(0,0,0) rot=(1,0,0;1.5708rad)
  Profile = -> Sketch042
  ReferenceAxis = -> Sketch042 [N_Axis]
  Reversed = true
  Suppressed = false
  Type = 0
FEATURE [PartDesign::Boolean] Boolean004
  BaseFeature = -> Pad022
  Group = -> [Body070]
  Suppressed = false
  Type = 2
  UsePlacement = false
FEATURE [Sketcher::SketchObject] Sketch043
  ArcFitTolerance = 0
  FullyConstrained = true
  MakeInternals = false
  MapMode = 5
  Placement = pos=(0,0,0) rot=(1,0,0;1.5708rad)
  sketch-geometry (2):
    g0: Circle CenterX=0 CenterY=0 CenterZ=0 NormalX=0 NormalY=0 NormalZ=1 AngleXU=0 Radius=41
    g1: Circle CenterX=0 CenterY=0 CenterZ=0 NormalX=0 NormalY=0 NormalZ=1 AngleXU=0 Radius=15
  constraints (4):
    c: Coincident(g0,g-1)
    c: Diameter(g0) = 82
    c: Coincident(g1,g0)
    c: Diameter(g1) = 30
FEATURE [PartDesign::Pocket] Pocket025
  BaseFeature = -> Boolean004
  Direction = (0,1,-2e-16)
  Length = 138
  Length2 = 5
  Profile = -> Sketch043
  ReferenceAxis = -> Sketch043 [N_Axis]
  Suppressed = false
  Type = 0
FEATURE [Sketcher::SketchObject] Sketch044
  ArcFitTolerance = 0
  AttachmentSupport = -> [XZ_Plane071]
  FullyConstrained = false
  MakeInternals = false
  MapMode = 5
  Placement = pos=(0,0,0) rot=(1,0,0;1.5708rad)
  sketch-geometry (3):
    g0: GeomPoint [constr] X=-87.5 Y=-1.47e-14 Z=0
    g1: Circle CenterX=0 CenterY=0 CenterZ=0 NormalX=0 NormalY=0 NormalZ=1 AngleXU=0 Radius=43
    g2: Circle CenterX=0 CenterY=0 CenterZ=0 NormalX=0 NormalY=0 NormalZ=1 AngleXU=0 Radius=47.5
  constraints (4):
    c: Coincident(g1,g-1)
    c: Coincident(g2,g1)
    c: Diameter(g1) = 86
    c: Diameter(g2) = 95
FEATURE [PartDesign::Pocket] Pocket026  label="Pocket002-ring002"
  BaseFeature = -> Pocket025
  Direction = (0,1,-2e-16)
  Length = 143
  Length2 = -141
  Profile = -> Sketch044
  ReferenceAxis = -> Sketch044 [N_Axis]
  Suppressed = false
  Type = 4
FEATURE [PartDesign::Pocket] Pocket027  label="Pocket003-ring003"
  BaseFeature = -> Pocket026
  Direction = (0,1,-2e-16)
  Length = 138
  Length2 = -136
  Profile = -> Sketch044
  ReferenceAxis = -> Sketch044 [N_Axis]
  Suppressed = false
  Type = 4
FEATURE [PartDesign::Pocket] Pocket028  label="Pocket004-komp-ring001"
  BaseFeature = -> Pocket027
  Direction = (0,1,-2e-16)
  Length = 55
  Length2 = -58
  Profile = -> Sketch044
  ReferenceAxis = -> Sketch044 [N_Axis]
  Suppressed = false
  Type = 4
FEATURE [Sketcher::SketchObject] Sketch049
  ArcFitTolerance = 0
  FullyConstrained = true
  MakeInternals = false
  MapMode = 5
  Placement = pos=(0,0,0) rot=(1,0,0;1.5708rad)
  sketch-geometry (1):
    g0: Circle CenterX=0 CenterY=0 CenterZ=0 NormalX=0 NormalY=0 NormalZ=1 AngleXU=0 Radius=30
  constraints (2):
    c: Coincident(g0,g-1)
    c: Diameter(g0) = 60
FEATURE [PartDesign::Pocket] Pocket030  label="Pocket023-conrod-polzun001"
  BaseFeature = -> Pocket028
  Direction = (0,1,-2e-16)
  Length = 110
  Length2 = 5
  Profile = -> Sketch049
  ReferenceAxis = -> Sketch049 [N_Axis]
  Suppressed = false
  Type = 0
FEATURE [PartDesign::Pocket] Pocket031  label="Pocket002-ring3"
  BaseFeature = -> Pocket030
  Direction = (0,1,-2e-16)
  Length = 63
  Length2 = -61
  Profile = -> Sketch044
  ReferenceAxis = -> Sketch044 [N_Axis]
  Suppressed = false
  Type = 4
FEATURE [Sketcher::SketchObject] Sketch052
  ArcFitTolerance = 0
  FullyConstrained = true
  MakeInternals = false
  MapMode = 5
  Placement = pos=(0,0,0) rot=(1,0,0;1.5708rad)
  sketch-geometry (1):
    g0: Circle CenterX=0 CenterY=0 CenterZ=0 NormalX=0 NormalY=0 NormalZ=1 AngleXU=0 Radius=11
  constraints (2):
    c: Coincident(g0,g-1)
    c: Diameter(g0) = 22
FEATURE [PartDesign::Pocket] Pocket032
  BaseFeature = -> Pocket031
  Direction = (0,1,-2e-16)
  Length = 130
  Length2 = 5
  Profile = -> Sketch052
  ReferenceAxis = -> Sketch052 [N_Axis]
  Suppressed = false
  Type = 4
FEATURE [PartDesign::Body] Body071  label="Поршень_2T_92mm"
  AllowCompound = false
  Group = -> [Sketch042,Pad022,Boolean004,Sketch043,Pocket025,Sketch044,Pocket026,Pocket027,Pocket028,Piston001,Sketch049,Pocket030,Pocket031,Sketch052,Pocket032]
  Origin = -> Origin072
  Tip = -> Pocket032
COMPONENT P17 — recipe-attached ("Цилиндр", modeled in this document).
Construction recipe (the document's own serialized feature program — sketch geometry with constraints, then the solid features built on it; lengths are millimeters unless a unit is written):

FEATURE [PartDesign::CoordinateSystem] Cylynder001
  AttacherType = Attacher::AttachEngine3D
  AttachmentSupport = -> [Body073]
  MapMode = 2
  Placement = pos=(0,0,25) rot=(0,0,1;0rad)
FEATURE [Sketcher::SketchObject] Sketch046
  ArcFitTolerance = 0
  AttachmentSupport = -> [XZ_Plane072]
  FullyConstrained = false
  MakeInternals = false
  MapMode = 5
  Placement = pos=(0,0,0) rot=(1,0,0;1.5708rad)
  sketch-geometry (12):
    g0: ArcOfCircle [constr] CenterX=-53 CenterY=1.3e-15 CenterZ=0 NormalX=0 NormalY=0 NormalZ=1 AngleXU=0 Radius=46 StartAngle=1.5708 EndAngle=4.71239
    g1: ArcOfCircle [constr] CenterX=0 CenterY=0 CenterZ=0 NormalX=0 NormalY=0 NormalZ=1 AngleXU=0 Radius=46 StartAngle=4.71239 EndAngle=7.85398
    g2: LineSegment [constr] StartX=-53 StartY=-46 StartZ=0 EndX=-7.1e-15 EndY=-46 EndZ=0
    g3: LineSegment [constr] StartX=1.41e-14 StartY=46 StartZ=0 EndX=-53 EndY=46 EndZ=0
    g4: LineSegment StartX=-222.305 StartY=100 StartZ=0 EndX=222.305 EndY=100 EndZ=0
    g5: LineSegment StartX=222.305 StartY=100 StartZ=0 EndX=222.305 EndY=-100 EndZ=0
    g6: LineSegment StartX=222.305 StartY=-100 StartZ=0 EndX=-222.305 EndY=-100 EndZ=0
    g7: LineSegment StartX=-222.305 StartY=-100 StartZ=0 EndX=-222.305 EndY=100 EndZ=0
    g8: Circle CenterX=-53 CenterY=1.3e-15 CenterZ=0 NormalX=0 NormalY=0 NormalZ=1 AngleXU=0 Radius=46
    g9: Circle [constr] CenterX=0 CenterY=0 CenterZ=0 NormalX=0 NormalY=0 NormalZ=1 AngleXU=0 Radius=46
    g10: Circle CenterX=53 CenterY=0 CenterZ=0 NormalX=0 NormalY=0 NormalZ=1 AngleXU=0 Radius=46
    g11: LineSegment [constr] StartX=1.41e-14 StartY=46 StartZ=0 EndX=53 EndY=46 EndZ=0
  constraints (28):
    c: Tangent(g0,g2) = -1.5708
    c: Tangent(g2,g1) = -1.5708
    c: Tangent(g1,g3) = -1.5708
    c: Tangent(g3,g0) = -1.5708
    c: Equal(g0,g1)
    c: Horizontal(g2)
    c: DistanceY(g0,g0) = 92
    c: Coincident(g4,g5)
    c: Coincident(g5,g6)
    c: Coincident(g6,g7)
    c: Coincident(g7,g4)
    c: Horizontal(g6)
    c: Vertical(g7)
    c: DistanceY(g5,g5) = 200
    c: Symmetric(g5,g4,g-1)
    c: Symmetric(g4,g4,g-2)
    c: Coincident(g8,g0)
    c: Coincident(g9,g1)
    c: Equal(g8,g0)
    c: Equal(g9,g1)
    c: Coincident(g9,g-1)
    c: PointOnObject(g10,g-1)
    c: Equal(g9,g10)
    c: Coincident(g11,g1)
    c: PointOnObject(g11,g10)
    c: Horizontal(g11)
    c: Equal(g3,g11)
    c: DistanceX(g8,g10) = 106
FEATURE [PartDesign::Pad] Pad023
  Direction = (0,-1,2e-16)
  Length = 300
  Length2 = 10
  Placement = pos=(0,0,0) rot=(1,0,0;1.5708rad)
  Profile = -> Sketch046
  ReferenceAxis = -> Sketch046 [N_Axis]
  Suppressed = false
  Type = 0
FEATURE [PartDesign::Boolean] Boolean005
  BaseFeature = -> Pad023
  Group = -> [Body073]
  Suppressed = false
  Type = 2
  UsePlacement = false
FEATURE [Sketcher::SketchObject] Sketch047
  ArcFitTolerance = 0
  AttachmentSupport = -> [XY_Plane071]
  FullyConstrained = true
  MakeInternals = false
  MapMode = 5
  sketch-geometry (2):
    g0: Circle CenterX=-137 CenterY=-90 CenterZ=0 NormalX=0 NormalY=0 NormalZ=1 AngleXU=0 Radius=30.5
    g1: Circle CenterX=137 CenterY=-90 CenterZ=0 NormalX=0 NormalY=0 NormalZ=1 AngleXU=0 Radius=30.5
  constraints (5):
    c: Diameter(g0) = 61
    c: Symmetric(g0,g1,g-2)
    c: DistanceY(g0,g-1) = 90
    c: DistanceX(g0,g1) = 274
    c: Equal(g1,g0)
FEATURE [Sketcher::SketchObject] Sketch048
  ArcFitTolerance = 0
  AttachmentSupport = -> [XY_Plane071]
  FullyConstrained = false
  MakeInternals = false
  MapMode = 5
  sketch-geometry (17):
    g0: LineSegment [constr] StartX=72.5228 StartY=-25.9373 StartZ=0 EndX=72.5228 EndY=-109 EndZ=0
    g1: LineSegment [constr] StartX=72.5228 StartY=-109 StartZ=0 EndX=-72.5228 EndY=-109 EndZ=0
    g2: LineSegment [constr] StartX=-72.5228 StartY=-109 StartZ=0 EndX=-72.5228 EndY=-25.9373 EndZ=0
    g3: LineSegment StartX=-72.5228 StartY=-25.9373 StartZ=0 EndX=-160.839 EndY=-25.9373 EndZ=0
    g4: LineSegment StartX=-160.839 StartY=-25.9373 StartZ=0 EndX=-160.839 EndY=-150.037 EndZ=0
    g5: LineSegment StartX=-160.839 StartY=-150.037 StartZ=0 EndX=-95 EndY=-174 EndZ=0
    g6: LineSegment StartX=-95 StartY=-174 StartZ=0 EndX=-95 EndY=-193.155 EndZ=0
    g7: LineSegment StartX=-95 StartY=-193.155 StartZ=0 EndX=-179.18 EndY=-162.516 EndZ=0
    g8: LineSegment StartX=-179.18 StartY=-162.516 StartZ=0 EndX=-179.18 EndY=-8.0171 EndZ=0
    g9: LineSegment StartX=-179.18 StartY=-8.0171 StartZ=0 EndX=179.18 EndY=-8.0171 EndZ=0
    g10: LineSegment StartX=179.18 StartY=-8.0171 StartZ=0 EndX=179.18 EndY=-156.131 EndZ=0
    g11: LineSegment StartX=179.18 StartY=-156.131 StartZ=0 EndX=95 EndY=-186.77 EndZ=0
    g12: LineSegment StartX=95 StartY=-186.77 StartZ=0 EndX=95 EndY=-174 EndZ=0
    g13: LineSegment StartX=95 StartY=-174 StartZ=0 EndX=160.839 EndY=-150.037 EndZ=0
    g14: LineSegment StartX=160.839 StartY=-150.037 StartZ=0 EndX=160.839 EndY=-25.9373 EndZ=0
    g15: LineSegment StartX=160.839 StartY=-25.9373 StartZ=0 EndX=72.5228 EndY=-25.9373 EndZ=0
    g16: LineSegment StartX=-72.5228 StartY=-25.9373 StartZ=0 EndX=72.5228 EndY=-25.9373 EndZ=0
  constraints (43):
    c: Coincident(g0,g1)
    c: Coincident(g1,g2)
    c: Vertical(g0)
    c: Vertical(g2)
    c: DistanceY(g0,g-1) = 109
    c: Symmetric(g1,g0,g-2)
    c: Coincident(g2,g3)
    c: Horizontal(g3)
    c: Coincident(g3,g4)
    c: Vertical(g4)
    c: Coincident(g4,g5)
    c: Coincident(g5,g6)
    c: Vertical(g6)
    c: Coincident(g6,g7)
    c: Coincident(g7,g8)
    c: Vertical(g8)
    c: Coincident(g8,g9)
    c: Coincident(g9,g10)
    c: Vertical(g10)
    c: Coincident(g10,g11)
    c: Coincident(g11,g12)
    c: Vertical(g12)
    c: Coincident(g12,g13)
    c: Coincident(g13,g14)
    c: Vertical(g14)
    c: Coincident(g14,g15)
    c: Coincident(g15,g0)
    c: Horizontal(g15)
    c: Symmetric(g8,g9,g-2)
    c: Equal(g3,g15)
    c: Parallel(g5,g7)
    c: Parallel(g13,g11)
    c: Distance(g12,g11) = 12
    c: Angle(g5) = -0.349066
    c: Angle(g13) = 0.349066
    c: Symmetric(g5,g12,g-2)
    c: DistanceX(g5,g12) = 190
    c: DistanceY(g5,g-1) = 174
    c: Block(g9)
    c: Distance(g5,g7) = 18
    c: Coincident(g16,g3)
    c: Coincident(g16,g15)
    c: Horizontal(g16)
FEATURE [PartDesign::Pocket] Pocket029
  BaseFeature = -> Boolean005
  Direction = (0,0,-1)
  Length = 60
  Length2 = 5
  Midplane = true
  Profile = -> Sketch048
  ReferenceAxis = -> Sketch048 [N_Axis]
  Suppressed = false
  Type = 0
FEATURE [Sketcher::SketchObject] Sketch050
  ArcFitTolerance = 0
  AttachmentSupport = -> [YZ_Plane072]
  FullyConstrained = false
  MakeInternals = false
  MapMode = 5
  Placement = pos=(0,0,0) rot=(0.57735,0.57735,0.57735;2.0944rad)
  sketch-geometry (4):
    g0: LineSegment StartX=-184.527 StartY=91.8627 StartZ=0 EndX=-217.963 EndY=0 EndZ=0
    g1: LineSegment StartX=-217.963 StartY=0 StartZ=0 EndX=-202 EndY=0 EndZ=0
    g2: LineSegment StartX=-202 StartY=0 StartZ=0 EndX=-168.565 EndY=91.8627 EndZ=0
    g3: LineSegment StartX=-168.565 StartY=91.8627 StartZ=0 EndX=-184.527 EndY=91.8627 EndZ=0
  constraints (11):
    c: Coincident(g0,g1)
    c: Horizontal(g1)
    c: Coincident(g1,g2)
    c: Coincident(g2,g3)
    c: Coincident(g3,g0)
    c: Horizontal(g3)
    c: Equal(g1,g3)
    c: Angle(g2) = 1.22173
    c: Distance(g1,g0) = 15
    c: PointOnObject(g1,g-1)
    c: DistanceX(g1,g-1) = 202
FEATURE [PartDesign::Body] Body072  label="Цилиндр"
  AllowCompound = false
  Group = -> [Sketch046,Pad023,Boolean005,Cylynder001,Sketch047,Sketch048,Pocket029,Sketch050]
  Origin = -> Origin073
  Placement = pos=(0,0,25) rot=(0,0,1;0rad)
  Tip = -> Pocket029
COMPONENT P18 — recipe-attached ("Body073", modeled in this document).
Construction recipe (the document's own serialized feature program — sketch geometry with constraints, then the solid features built on it; lengths are millimeters unless a unit is written):

FEATURE [Sketcher::SketchObject] Sketch045
  ArcFitTolerance = 0
  AttachmentSupport = -> [XY_Plane072]
  FullyConstrained = true
  MakeInternals = false
  MapMode = 5
  sketch-geometry (11):
    g0: LineSegment [constr] StartX=-120 StartY=252 StartZ=0 EndX=120 EndY=252 EndZ=0
    g1: LineSegment [constr] StartX=120 StartY=252 StartZ=0 EndX=120 EndY=-252 EndZ=0
    g2: LineSegment StartX=120 StartY=-252 StartZ=0 EndX=-120 EndY=-252 EndZ=0
    g3: LineSegment [constr] StartX=-120 StartY=-252 StartZ=0 EndX=-120 EndY=252 EndZ=0
    g4: LineSegment [constr] StartX=-120 StartY=252 StartZ=0 EndX=-120 EndY=75.5 EndZ=0
    g5: LineSegment [constr] StartX=-120 StartY=75.5 StartZ=0 EndX=120 EndY=75.5 EndZ=0
    g6: LineSegment [constr] StartX=120 StartY=75.5 StartZ=0 EndX=120 EndY=252 EndZ=0
    g7: LineSegment StartX=-120 StartY=-252 StartZ=0 EndX=-120 EndY=-75.5 EndZ=0
    g8: LineSegment StartX=-120 StartY=-75.5 StartZ=0 EndX=120 EndY=-75.5 EndZ=0
    g9: LineSegment [constr] StartX=120 StartY=-75.5 StartZ=0 EndX=120 EndY=-252 EndZ=0
    g10: LineSegment StartX=120 StartY=-75.5 StartZ=0 EndX=120 EndY=-252 EndZ=0
  constraints (28):
    c: Coincident(g0,g1)
    c: Coincident(g1,g2)
    c: Coincident(g2,g3)
    c: Coincident(g3,g0)
    c: Horizontal(g2)
    c: Vertical(g1)
    c: Symmetric(g0,g0,g-2)
    c: Symmetric(g0,g2,g-1)
    c: Coincident(g0,g4)
    c: PointOnObject(g4,g3)
    c: Coincident(g4,g5)
    c: PointOnObject(g5,g1)
    c: Horizontal(g5)
    c: Coincident(g5,g6)
    c: Coincident(g6,g0)
    c: Coincident(g2,g7)
    c: PointOnObject(g7,g3)
    c: Coincident(g7,g8)
    c: PointOnObject(g8,g1)
    c: Horizontal(g8)
    c: Coincident(g8,g9)
    c: Coincident(g9,g2)
    c: Equal(g9,g6)
    c: DistanceX(g2,g2) = 240
    c: Coincident(g10,g8)
    c: Coincident(g10,g2)
    c: DistanceY(g2,g-1) = 252
    c: DistanceY(g7,g7) = 176.5
FEATURE [PartDesign::Pad] Pad024
  Direction = (0,0,1)
  Length = 28
  Length2 = 78
  Midplane = true
  Profile = -> Sketch045
  ReferenceAxis = -> Sketch045 [N_Axis]
  Suppressed = false
  Type = 4
FEATURE [PartDesign::Body] Body073
  AllowCompound = false
  Group = -> [Sketch045,Pad024]
  Origin = -> Origin074
  Placement = pos=(0,0,25) rot=(0,0,1;0rad)
  Tip = -> Pad024
COMPONENT P19 — recipe-attached ("корпус_нижний", modeled in this document).
Construction recipe (the document's own serialized feature program — sketch geometry with constraints, then the solid features built on it; lengths are millimeters unless a unit is written):

FEATURE [Sketcher::SketchObject] Sketch060
  ArcFitTolerance = 0
  FullyConstrained = true
  MakeInternals = false
  Placement = pos=(0,0,0) rot=(1,0,0;3.14159rad)
  expr: Constraints[11] = <<Dim_table>>.crank_dia1 + <<Dim_table>>.zazor
  expr: Constraints[14] = <<Dim_table>>.crank_dia2
  expr: Constraints[15] = <<Dim_table>>.inter_shaft_len / 2
  expr: Constraints[6] = <<Dim_table>>.inter_shaft_len
  expr: Constraints[7] = <<Dim_table>>.crank_dia1 * 1.5
  sketch-geometry (7):
    g0: ArcOfCircle CenterX=0 CenterY=0 CenterZ=0 NormalX=0 NormalY=0 NormalZ=1 AngleXU=0 Radius=18.75 StartAngle=1.5708 EndAngle=4.71239
    g1: ArcOfCircle CenterX=100 CenterY=-1.6e-15 CenterZ=0 NormalX=0 NormalY=0 NormalZ=1 AngleXU=0 Radius=18.75 StartAngle=4.71239 EndAngle=7.85398
    g2: LineSegment StartX=-3.4e-15 StartY=-18.75 StartZ=0 EndX=100 EndY=-18.75 EndZ=0
    g3: LineSegment StartX=100 StartY=18.75 StartZ=0 EndX=1.42e-14 EndY=18.75 EndZ=0
    g4: Circle CenterX=0 CenterY=0 CenterZ=0 NormalX=0 NormalY=0 NormalZ=1 AngleXU=0 Radius=12.75
    g5: Circle CenterX=100 CenterY=-1.6e-15 CenterZ=0 NormalX=0 NormalY=0 NormalZ=1 AngleXU=0 Radius=12.75
    g6: Circle CenterX=50 CenterY=0 CenterZ=0 NormalX=0 NormalY=0 NormalZ=1 AngleXU=0 Radius=12.5
  constraints (16):
    c: Tangent(g0,g2) = -1.5708
    c: Tangent(g2,g1) = -1.5708
    c: Tangent(g1,g3) = -1.5708
    c: Tangent(g3,g0) = -1.5708
    c: Equal(g0,g1)
    c: Horizontal(g2)
    c: DistanceX(g0,g1) = 100
    c: Diameter(g0) = 37.5
    c: Coincident(g4,g0)
    c: Coincident(g5,g1)
    c: Equal(g4,g5)
    c: Diameter(g4) = 25.5
    c: Coincident(g0,g-1)
    c: PointOnObject(g6,g-1)
    c: Diameter(g6) = 25
    c: DistanceX(g0,g6) = 50
FEATURE [Sketcher::SketchObject] Sketch064
  ArcFitTolerance = 0
  FullyConstrained = true
  MakeInternals = false
  Placement = pos=(0,0,0) rot=(1,0,0;3.14159rad)
  expr: Constraints[1] = <<Dim_table>>.inter_shaft_len * 1.2
  sketch-geometry (1):
    g0: Circle CenterX=0 CenterY=0 CenterZ=0 NormalX=0 NormalY=0 NormalZ=1 AngleXU=0 Radius=60
  constraints (2):
    c: Coincident(g0,g-1)
    c: Diameter(g0) = 120
FEATURE [Sketcher::SketchObject] Sketch074
  ArcFitTolerance = 0
  AttachmentSupport = -> [XY_Plane076]
  FullyConstrained = true
  MakeInternals = false
  MapMode = 5
  expr: Constraints[14] = <<Dim_table>>.ecc_dia * 1.2
  expr: Constraints[33] = <<Dim_table>>.crank_dia2
  expr: Constraints[34] = <<Dim_table>>.inter_shaft_len * 2.2
  expr: Constraints[46] = <<Dim_table>>.axle_hole_dia
  expr: Constraints[48] = 32
  expr: Constraints[53] = <<Dim_table>>.inter_shaft_len * 1.8
  sketch-geometry (25):
    g0: LineSegment [constr] StartX=-42 StartY=-90 StartZ=0 EndX=42 EndY=-90 EndZ=0
    g1: LineSegment [constr] StartX=90 StartY=-42 StartZ=0 EndX=90 EndY=42 EndZ=0
    g2: LineSegment [constr] StartX=42 StartY=90 StartZ=0 EndX=-42 EndY=90 EndZ=0
    g3: LineSegment [constr] StartX=-90 StartY=42 StartZ=0 EndX=-90 EndY=-42 EndZ=0
    g4: ArcOfCircle [constr] CenterX=-42 CenterY=42 CenterZ=0 NormalX=0 NormalY=0 NormalZ=1 AngleXU=0 Radius=48 StartAngle=1.5708 EndAngle=3.14159
    g5: ArcOfCircle [constr] CenterX=42 CenterY=42 CenterZ=0 NormalX=0 NormalY=0 NormalZ=1 AngleXU=0 Radius=48 StartAngle=1e-16 EndAngle=1.5708
    g6: ArcOfCircle [constr] CenterX=-42 CenterY=-42 CenterZ=0 NormalX=0 NormalY=0 NormalZ=1 AngleXU=0 Radius=48 StartAngle=3.14159 EndAngle=4.71239
    g7: ArcOfCircle [constr] CenterX=42 CenterY=-42 CenterZ=0 NormalX=0 NormalY=0 NormalZ=1 AngleXU=0 Radius=48 StartAngle=4.71239 EndAngle=6.28319
    g8: LineSegment [constr] StartX=-90 StartY=-42 StartZ=0 EndX=90 EndY=42 EndZ=0
    g9: GeomPoint [constr] X=0 Y=0 Z=0
    g10: ArcOfCircle CenterX=-97.5 CenterY=97.5 CenterZ=0 NormalX=0 NormalY=0 NormalZ=1 AngleXU=0 Radius=12.5 StartAngle=1.5708 EndAngle=3.14159
    g11: LineSegment StartX=97.5 StartY=110 StartZ=0 EndX=-97.5 EndY=110 EndZ=0
    g12: ArcOfCircle CenterX=97.5 CenterY=97.5 CenterZ=0 NormalX=0 NormalY=0 NormalZ=1 AngleXU=0 Radius=12.5 StartAngle=4.16e-13 EndAngle=1.5708
    g13: LineSegment StartX=110 StartY=-97.5 StartZ=0 EndX=110 EndY=97.5 EndZ=0
    g14: ArcOfCircle CenterX=97.5 CenterY=-97.5 CenterZ=0 NormalX=0 NormalY=0 NormalZ=1 AngleXU=0 Radius=12.5 StartAngle=4.71239 EndAngle=6.28319
    g15: LineSegment StartX=-97.5 StartY=-110 StartZ=0 EndX=97.5 EndY=-110 EndZ=0
    g16: ArcOfCircle CenterX=-97.5 CenterY=-97.5 CenterZ=0 NormalX=0 NormalY=0 NormalZ=1 AngleXU=0 Radius=12.5 StartAngle=3.14159 EndAngle=4.71239
    g17: LineSegment StartX=-110 StartY=97.5 StartZ=0 EndX=-110 EndY=-97.5 EndZ=0
    g18: LineSegment [constr] StartX=-97.5 StartY=110 StartZ=0 EndX=97.5 EndY=-110 EndZ=0
    g19: GeomPoint [constr] X=0 Y=0 Z=0
    g20: Circle CenterX=-97.5 CenterY=97.5 CenterZ=0 NormalX=0 NormalY=0 NormalZ=1 AngleXU=0 Radius=2.5
    g21: Circle CenterX=97.5 CenterY=97.5 CenterZ=0 NormalX=0 NormalY=0 NormalZ=1 AngleXU=0 Radius=2.5
    g22: Circle CenterX=-97.5 CenterY=-97.5 CenterZ=0 NormalX=0 NormalY=0 NormalZ=1 AngleXU=0 Radius=2.5
    g23: Circle CenterX=97.5 CenterY=-97.5 CenterZ=0 NormalX=0 NormalY=0 NormalZ=1 AngleXU=0 Radius=2.5
    g24: Circle CenterX=0 CenterY=0 CenterZ=0 NormalX=0 NormalY=0 NormalZ=1 AngleXU=0 Radius=16
  constraints (54):
    c: Horizontal(g0)
    c: Horizontal(g2)
    c: Vertical(g1)
    c: Vertical(g3)
    c: Tangent(g2,g4) = -1.5708
    c: Tangent(g3,g4) = -1.5708
    c: Tangent(g2,g5) = -1.5708
    c: Tangent(g1,g5) = -1.5708
    c: Tangent(g3,g6) = -1.5708
    c: Tangent(g0,g6) = -1.5708
    c: Tangent(g0,g7) = -1.5708
    c: Tangent(g1,g7) = -1.5708
    c: Equal(g4,g5)
    c: Equal(g5,g7)
    c: Diameter(g4) = 96
    c: Symmetric(g2,g0,g-1)
    c: Coincident(g8,g3)
    c: Coincident(g8,g1)
    c: PointOnObject(g9,g8)
    c: Horizontal(g15)
    c: Horizontal(g11)
    c: Vertical(g13)
    c: Vertical(g17)
    c: Tangent(g11,g10) = -1.5708
    c: Tangent(g17,g10) = -1.5708
    c: Tangent(g11,g12) = -1.5708
    c: Tangent(g13,g12) = -1.5708
    c: Tangent(g17,g16) = -1.5708
    c: Tangent(g15,g16) = -1.5708
    c: Tangent(g15,g14) = -1.5708
    c: Tangent(g13,g14) = -1.5708
    c: Equal(g10,g12)
    c: Equal(g12,g14)
    c: Diameter(g10) = 25
    c: DistanceY(g15,g11) = 220
    c: Symmetric(g10,g16,g-1)
    c: Coincident(g18,g10)
    c: Coincident(g18,g14)
    c: PointOnObject(g19,g18)
    c: Coincident(g20,g10)
    c: Coincident(g21,g12)
    c: Coincident(g22,g16)
    c: Coincident(g23,g14)
    c: Equal(g22,g23)
    c: Equal(g23,g21)
    c: Equal(g21,g20)
    c: Diameter(g20) = 5
    c: Coincident(g24,g9)
    c: Diameter(g24) = 32
    c: Coincident(g9,g19)
    c: Coincident(g-1,g9)
    c: Equal(g11,g13)
    c: Equal(g2,g1)
    c: DistanceX(g3,g1) = 180
FEATURE [PartDesign::CoordinateSystem] Shtok004
  AttacherType = Attacher::AttachEngine3D
  AttachmentSupport = -> [Sketch074]
  MapMode = 2
FEATURE [PartDesign::Pad] Pad042
  Direction = (0,0,1)
  Length = 15
  Length2 = 10
  Profile = -> Sketch074
  ReferenceAxis = -> Sketch074 [N_Axis]
  Reversed = true
  Suppressed = false
  Type = 0
FEATURE [PartDesign::Pad] Pad043
  BaseFeature = -> Pad042
  Direction = (0,-1e-16,-1)
  Length = 25
  Length2 = 10
  Profile = -> Sketch060
  ReferenceAxis = -> Sketch060 [N_Axis]
  Suppressed = false
  Type = 0
FEATURE [PartDesign::Pocket] Pocket036
  BaseFeature = -> Pad043
  Direction = (0,1e-16,1)
  Length = 10.5
  Length2 = 5
  Profile = -> Sketch064
  ReferenceAxis = -> Sketch064 [N_Axis]
  Reversed = true
  Suppressed = false
  Type = 0
FEATURE [PartDesign::Body] Body076  label="корпус_нижний"
  AllowCompound = false
  Group = -> [Shtok004,Sketch060,Sketch064,Sketch074,Pad042,Pad043,Pocket036]
  Origin = -> Origin077
  Tip = -> Pocket036
COMPONENT P20 — recipe-attached ("проставка_корпуса", modeled in this document).
Construction recipe (the document's own serialized feature program — sketch geometry with constraints, then the solid features built on it; lengths are millimeters unless a unit is written):

FEATURE [Sketcher::SketchObject] Sketch058
  ArcFitTolerance = 0
  AttachmentSupport = -> [XY_Plane077]
  FullyConstrained = false
  MakeInternals = false
  MapMode = 5
  sketch-geometry (32):
    g0: LineSegment [constr] StartX=-103 StartY=-65 StartZ=0 EndX=103 EndY=-65 EndZ=0
    g1: LineSegment [constr] StartX=103 StartY=-65 StartZ=0 EndX=103 EndY=65 EndZ=0
    g2: LineSegment [constr] StartX=103 StartY=65 StartZ=0 EndX=-103 EndY=65 EndZ=0
    g3: LineSegment [constr] StartX=-103 StartY=65 StartZ=0 EndX=-103 EndY=-65 EndZ=0
    g4: LineSegment [constr] StartX=-99 StartY=69.5 StartZ=0 EndX=99 EndY=69.5 EndZ=0
    g5: LineSegment [constr] StartX=-103 StartY=65 StartZ=0 EndX=-103 EndY=65.5 EndZ=0
    g6: LineSegment [constr] StartX=103 StartY=65.5 StartZ=0 EndX=103 EndY=65 EndZ=0
    g7: ArcOfCircle [constr] CenterX=-99 CenterY=65.5 CenterZ=0 NormalX=0 NormalY=0 NormalZ=1 AngleXU=0 Radius=4 StartAngle=1.5708 EndAngle=3.14159
    g8: ArcOfCircle [constr] CenterX=99 CenterY=65.5 CenterZ=0 NormalX=0 NormalY=0 NormalZ=1 AngleXU=0 Radius=4 StartAngle=-9e-16 EndAngle=1.5708
    g9: ArcOfCircle [constr] CenterX=-99 CenterY=-65.5 CenterZ=0 NormalX=0 NormalY=0 NormalZ=1 AngleXU=0 Radius=4 StartAngle=3.14159 EndAngle=4.71239
    g10: LineSegment [constr] StartX=-103 StartY=-65 StartZ=0 EndX=-103 EndY=-65.5 EndZ=0
    g11: LineSegment [constr] StartX=-99 StartY=-69.5 StartZ=0 EndX=99 EndY=-69.5 EndZ=0
    g12: ArcOfCircle [constr] CenterX=99 CenterY=-65.5 CenterZ=0 NormalX=0 NormalY=0 NormalZ=1 AngleXU=0 Radius=4 StartAngle=4.71239 EndAngle=6.28319
    g13: LineSegment [constr] StartX=103 StartY=-65.5 StartZ=0 EndX=103 EndY=-65 EndZ=0
    g14: Circle CenterX=-95 CenterY=55 CenterZ=0 NormalX=0 NormalY=0 NormalZ=1 AngleXU=0 Radius=3
    g15: Circle [constr] CenterX=95 CenterY=55 CenterZ=0 NormalX=0 NormalY=0 NormalZ=1 AngleXU=0 Radius=3
    g16: Circle [constr] CenterX=-95 CenterY=-55 CenterZ=0 NormalX=0 NormalY=0 NormalZ=1 AngleXU=0 Radius=3
    g17: Circle [constr] CenterX=95 CenterY=-55 CenterZ=0 NormalX=0 NormalY=0 NormalZ=1 AngleXU=0 Radius=3
    g18: Circle [constr] CenterX=0 CenterY=0 CenterZ=0 NormalX=0 NormalY=0 NormalZ=1 AngleXU=0 Radius=32.25
    g19: LineSegment [constr] StartX=-103 StartY=-65 StartZ=0 EndX=-91.9993 EndY=-65 EndZ=0
    g20: LineSegment [constr] StartX=-91.9993 StartY=-65 StartZ=0 EndX=-91.9993 EndY=-49.9993 EndZ=0
    g21: LineSegment [constr] StartX=-91.9993 StartY=-49.9993 StartZ=0 EndX=-103 EndY=-49.9993 EndZ=0
    g22: LineSegment [constr] StartX=-103 StartY=-49.9993 StartZ=0 EndX=-103 EndY=-65 EndZ=0
    g23: LineSegment [constr] StartX=103 StartY=-65 StartZ=0 EndX=91.9993 EndY=-65 EndZ=0
    g24: LineSegment [constr] StartX=91.9993 StartY=-65 StartZ=0 EndX=91.9993 EndY=-49.9993 EndZ=0
    g25: LineSegment [constr] StartX=91.9993 StartY=-49.9993 StartZ=0 EndX=103 EndY=-49.9993 EndZ=0
    g26: LineSegment [constr] StartX=103 StartY=-49.9993 StartZ=0 EndX=103 EndY=-65 EndZ=0
    g27: LineSegment [constr] StartX=103 StartY=65 StartZ=0 EndX=91.9993 EndY=65 EndZ=0
    g28: LineSegment [constr] StartX=91.9993 StartY=65 StartZ=0 EndX=91.9993 EndY=49.9993 EndZ=0
    g29: LineSegment [constr] StartX=91.9993 StartY=49.9993 StartZ=0 EndX=103 EndY=49.9993 EndZ=0
    g30: LineSegment [constr] StartX=103 StartY=49.9993 StartZ=0 EndX=103 EndY=65 EndZ=0
    g31: Circle CenterX=-95 CenterY=55 CenterZ=0 NormalX=0 NormalY=0 NormalZ=1 AngleXU=0 Radius=8
  constraints (75):
    c: Coincident(g0,g1)
    c: Coincident(g1,g2)
    c: Coincident(g2,g3)
    c: Coincident(g3,g0)
    c: Horizontal(g0)
    c: Vertical(g1)
    c: Symmetric(g2,g1,g-2)
    c: Symmetric(g2,g0,g-1)
    c: DistanceX(g2,g2) = 206
    c: DistanceY(g1,g1) = 130
    c: Coincident(g5,g3)
    c: Coincident(g6,g1)
    c: Tangent(g5,g7) = 1.5708
    c: Tangent(g4,g7) = 1.5708
    c: Tangent(g4,g8) = 1.5708
    c: Tangent(g6,g8) = 1.5708
    c: Vertical(g5)
    c: Vertical(g6)
    c: Symmetric(g7,g8,g-2)
    c: DistanceY(g1,g4) = 4.5
    c: Radius(g8) = 4
    c: Tangent(g10,g9) = -1.5708
    c: Tangent(g11,g9) = -1.5708
    c: Tangent(g11,g12) = -1.5708
    c: Vertical(g10)
    c: Symmetric(g9,g12,g-2)
    c: Symmetric(g9,g7,g-1)
    c: Coincident(g10,g3)
    c: Coincident(g13,g1)
    c: Vertical(g13)
    c: Equal(g13,g10)
    c: Coincident(g12,g13)
    c: Equal(g14,g15)
    c: Equal(g15,g17)
    c: Equal(g17,g16)
    c: Diameter(g15) = 6
    c: Symmetric(g14,g15,g-2)
    c: Symmetric(g16,g17,g-2)
    c: Symmetric(g16,g14,g-1)
    c: DistanceY(g16,g14) = 110
    c: DistanceX(g16,g17) = 190
    c: Coincident(g18,g-1)
    c: Diameter(g18) = 64.5
    c: Coincident(g19,g20)
    c: Coincident(g20,g21)
    c: Coincident(g21,g22)
    c: Coincident(g22,g19)
    c: Horizontal(g19)
    c: Horizontal(g21)
    c: Vertical(g20)
    c: Vertical(g22)
    c: Coincident(g19,g0)
    c: Coincident(g23,g24)
    c: Coincident(g24,g25)
    c: Coincident(g25,g26)
    c: Coincident(g26,g23)
    c: Horizontal(g23)
    c: Horizontal(g25)
    c: Vertical(g24)
    c: Vertical(g26)
    c: Coincident(g23,g0)
    c: Coincident(g27,g28)
    c: Coincident(g28,g29)
    c: Coincident(g29,g30)
    c: Coincident(g30,g27)
    c: Horizontal(g27)
    c: Horizontal(g29)
    c: Vertical(g28)
    c: Vertical(g30)
    c: Coincident(g27,g1)
    c: Equal(g25,g29)
    c: Equal(g28,g24)
    c: Equal(g24,g20)
    c: Coincident(g31,g14)
    c: Tangent(g31,g3)
FEATURE [PartDesign::Pad] Pad029
  Direction = (0,0,1)
  Length = 25
  Length2 = 28.5
  Midplane = true
  Profile = -> Sketch058
  ReferenceAxis = -> Sketch058 [N_Axis]
  Suppressed = false
  Type = 4
FEATURE [PartDesign::CoordinateSystem] Shtok005
  AttacherType = Attacher::AttachEngine3D
  AttachmentSupport = -> [Sketch058]
  MapMode = 2
FEATURE [PartDesign::Body] Body077  label="проставка_корпуса"
  AllowCompound = false
  Group = -> [Sketch058,Pad029,Shtok005]
  Origin = -> Origin078
  Tip = -> Pad029
COMPONENT P21 — recipe-attached ("crank_gear_01", modeled in this document).
Construction recipe (the document's own serialized feature program — sketch geometry with constraints, then the solid features built on it; lengths are millimeters unless a unit is written):

FEATURE [PartDesign::FeatureBase] BaseFeature
  BaseFeature = -> InvoluteGear006
  Suppressed = false
FEATURE [PartDesign::CoordinateSystem] Local_CS005
  AttacherType = Attacher::AttachEngine3D
  AttachmentOffset = pos=(0,0,0) rot=(0,0,1;0.279253rad)
  AttachmentSupport = -> [BaseFeature]
  MapMode = 2
  Placement = pos=(0,0,0) rot=(0,0,1;0.279253rad)
FEATURE [PartDesign::AdditiveCylinder] Cylinder004
  Angle = 360
  AttacherType = Attacher::AttachEngine3D
  AttachmentOffset = pos=(0,0,-0.5) rot=(0,0,1;0rad)
  AttachmentSupport = -> [BaseFeature]
  BaseFeature = -> BaseFeature
  FirstAngle = 0
  Height = 11
  MapMode = 2
  Placement = pos=(0,0,-0.5) rot=(0,0,1;0rad)
  Radius = 17
  Refine = true
  SecondAngle = 0
  Suppressed = false
FEATURE [PartDesign::SubtractiveCylinder] Cylinder005
  Angle = 360
  AttacherType = Attacher::AttachEngine3D
  AttachmentOffset = pos=(0,0,-3) rot=(0,0,1;0rad)
  AttachmentSupport = -> [BaseFeature]
  BaseFeature = -> Cylinder004
  FirstAngle = 0
  Height = 15
  MapMode = 2
  Placement = pos=(0,0,-3) rot=(0,0,1;0rad)
  Radius = 12.75
  Refine = true
  SecondAngle = 0
  Suppressed = false
FEATURE [PartDesign::Body] Body087  label="crank_gear_01"
  AllowCompound = false
  BaseFeature = -> InvoluteGear006
  Group = -> [BaseFeature,Local_CS005,Cylinder004,Cylinder005]
  Origin = -> Origin090
  Tip = -> Cylinder005
COMPONENT P22 — recipe-attached ("crank_int_gear_01", modeled in this document).
Construction recipe (the document's own serialized feature program — sketch geometry with constraints, then the solid features built on it; lengths are millimeters unless a unit is written):

FEATURE [PartDesign::FeatureBase] BaseFeature001
  BaseFeature = -> InternalInvoluteGear001
  Suppressed = false
FEATURE [PartDesign::CoordinateSystem] Local_CS004
  AttacherType = Attacher::AttachEngine3D
  AttachmentSupport = -> [BaseFeature001]
  MapMode = 2
FEATURE [PartDesign::Body] Body088  label="crank_int_gear_01"
  AllowCompound = false
  BaseFeature = -> InternalInvoluteGear001
  Group = -> [BaseFeature001,Local_CS004]
  Origin = -> Origin091
  Tip = -> BaseFeature001
COMPONENT P23 — recipe-attached ("Шейка_и_щека_задняя", modeled in this document).
Construction recipe (the document's own serialized feature program — sketch geometry with constraints, then the solid features built on it; lengths are millimeters unless a unit is written):

FEATURE [Sketcher::SketchObject] Sketch071
  ArcFitTolerance = 0
  FullyConstrained = true
  MakeInternals = false
  MapMode = 5
  expr: Constraints[0] = <<Dim_table>>.crank_dia2
  expr: Constraints[3] = <<Dim_table>>.axle_hole_dia
  sketch-geometry (2):
    g0: Circle CenterX=0 CenterY=0 CenterZ=0 NormalX=0 NormalY=0 NormalZ=1 AngleXU=0 Radius=12.5
    g1: Circle CenterX=0 CenterY=0 CenterZ=0 NormalX=0 NormalY=0 NormalZ=1 AngleXU=0 Radius=2.5
  constraints (4):
    c: Diameter(g0) = 25
    c: Coincident(g0,g-1)
    c: Coincident(g1,g0)
    c: Diameter(g1) = 5
FEATURE [PartDesign::Pad] Pad039
  Direction = (0,0,1)
  Length = 26
  Length2 = 10
  Profile = -> Sketch071
  ReferenceAxis = -> Sketch071 [N_Axis]
  Suppressed = false
  Type = 0
FEATURE [Sketcher::SketchObject] Sketch072
  ArcFitTolerance = 0
  AttachmentSupport = -> [XY_Plane094]
  FullyConstrained = true
  MakeInternals = false
  MapMode = 5
  expr: Constraints[17] = <<Dim_table>>.fillet_r
  expr: Constraints[18] = <<Dim_table>>.fillet_r
  expr: Constraints[23] = <<Dim_table>>.axle_hole_dia
  expr: Constraints[24] = 70
  expr: Constraints[25] = <<Dim_table>>.crank_dia2 * 1.5
  expr: Constraints[26] = <<Dim_table>>.crank_len
  sketch-geometry (14):
    g0: ArcOfCircle CenterX=0 CenterY=0 CenterZ=0 NormalX=0 NormalY=0 NormalZ=1 AngleXU=0 Radius=52.5 StartAngle=0.0396143 EndAngle=3.10198
    g1: ArcOfCircle CenterX=3e-16 CenterY=-21.25 CenterZ=0 NormalX=0 NormalY=0 NormalZ=1 AngleXU=0 Radius=18.75 StartAngle=3.49066 EndAngle=5.93412
    g2: LineSegment [constr] StartX=-17.6192 StartY=-27.6629 StartZ=0 EndX=17.6192 EndY=-27.6629 EndZ=0
    g3: LineSegment StartX=-50.4604 StartY=0 StartZ=0 EndX=-29.0881 EndY=0 EndZ=0
    g4: LineSegment StartX=-27.2087 StartY=-1.31596 StartZ=0 EndX=-17.6192 EndY=-27.6629 EndZ=0
    g5: LineSegment StartX=17.6192 StartY=-27.6629 StartZ=0 EndX=27.2087 EndY=-1.31596 EndZ=0
    g6: LineSegment StartX=29.0881 StartY=2.9e-15 StartZ=0 EndX=50.4604 EndY=2.9e-15 EndZ=0
    g7: ArcOfCircle CenterX=-29.0881 CenterY=-2 CenterZ=0 NormalX=0 NormalY=0 NormalZ=1 AngleXU=0 Radius=2 StartAngle=0.349066 EndAngle=1.5708
    g8: ArcOfCircle CenterX=29.0881 CenterY=-2 CenterZ=0 NormalX=0 NormalY=0 NormalZ=1 AngleXU=0 Radius=2 StartAngle=1.5708 EndAngle=2.79253
    g9: ArcOfCircle CenterX=50.4604 CenterY=2 CenterZ=0 NormalX=0 NormalY=0 NormalZ=1 AngleXU=0 Radius=2 StartAngle=4.71239 EndAngle=6.3228
    g10: ArcOfCircle CenterX=-50.4604 CenterY=2 CenterZ=0 NormalX=0 NormalY=0 NormalZ=1 AngleXU=0 Radius=2 StartAngle=3.10198 EndAngle=4.71239
    g11: Circle [constr] CenterX=0 CenterY=0 CenterZ=0 NormalX=0 NormalY=0 NormalZ=1 AngleXU=0 Radius=52.5
    g12: Circle CenterX=0 CenterY=0 CenterZ=0 NormalX=0 NormalY=0 NormalZ=1 AngleXU=0 Radius=2.5
    g13: Circle CenterX=3e-16 CenterY=-21.25 CenterZ=0 NormalX=0 NormalY=0 NormalZ=1 AngleXU=0 Radius=2.5
  constraints (31):
    c: Coincident(g2,g1)
    c: Coincident(g2,g1)
    c: Horizontal(g2)
    c: Horizontal(g3)
    c: Horizontal(g6)
    c: Tangent(g4,g1) = -1.5708
    c: Tangent(g5,g1) = -1.5708
    c: Tangent(g3,g7) = 1.5708
    c: Tangent(g4,g7) = 1.5708
    c: Tangent(g6,g8) = 1.5708
    c: Tangent(g5,g8) = 1.5708
    c: Tangent(g6,g9) = -1.5708
    c: Tangent(g0,g9) = -1.5708
    c: Tangent(g0,g10) = -1.5708
    c: Tangent(g3,g10) = -1.5708
    c: Symmetric(g7,g8,g-2)
    c: Symmetric(g10,g9,g-2)
    c: Radius(g10) = 2
    c: Radius(g7) = 2
    c: Coincident(g0,g-1)
    c: Coincident(g11,g0)
    c: Diameter(g11) = 105
    c: Coincident(g12,g11)
    c: Diameter(g12) = 5
    c: Angle(g5) = 1.22173
    c: Diameter(g1) = 37.5
    c: DistanceY(g1,g12) = 21.25
    c: PointOnObject(g3,g-1)
    c: Coincident(g13,g1)
    c: Equal(g13,g12)
    c: Equal(g0,g11)
FEATURE [PartDesign::Pad] Pad040
  BaseFeature = -> Pad039
  Direction = (0,0,1)
  Length = 15
  Length2 = 10
  Profile = -> Sketch072
  ReferenceAxis = -> Sketch072 [N_Axis]
  Reversed = true
  Suppressed = false
  Type = 0
FEATURE [PartDesign::Chamfer] Chamfer001
  Angle = 45
  Base = -> Pad040 [Edge14]
  BaseFeature = -> Pad040
  ChamferType = 0
  FlipDirection = false
  Size = 1.5
  Size2 = 1
  SupportTransform = false
  Suppressed = false
  UseAllEdges = false
FEATURE [PartDesign::Body] Body090  label="Шейка_и_щека_задняя"
  AllowCompound = false
  Group = -> [Sketch071,Pad039,Sketch072,Pad040,Chamfer001]
  Origin = -> Origin093
  Placement = pos=(0,0,-6.5) rot=(0,0,1;0rad)
  Tip = -> Chamfer001
COMPONENT P24 — recipe-attached ("Шейка_и_щека_задняя_cl", modeled in this document).
Construction recipe (the document's own serialized feature program — sketch geometry with constraints, then the solid features built on it; lengths are millimeters unless a unit is written):

FEATURE [PartDesign::FeatureBase] Clone
  BaseFeature = -> Cut
  Suppressed = false
FEATURE [PartDesign::CoordinateSystem] LCS_2
  AttacherType = Attacher::AttachEngine3D
  AttachmentSupport = -> [Cut]
  MapMode = 11
  Placement = pos=(0,0,-21.5) rot=(0,0,1;1.5708rad)
FEATURE [PartDesign::Fillet] Fillet001
  Base = -> Clone [Edge12]
  BaseFeature = -> Clone
  Radius = 0.25
  Refine = true
  SupportTransform = false
  Suppressed = false
  UseAllEdges = false
FEATURE [PartDesign::Body] Body091  label="Шейка_и_щека_задняя_cl"
  AllowCompound = false
  Group = -> [Clone,LCS_2,Fillet001]
  Origin = -> Origin094
  Tip = -> Fillet001
COMPONENT P25 — recipe-attached ("проставка_корпуса_штока1", modeled in this document).
Construction recipe (the document's own serialized feature program — sketch geometry with constraints, then the solid features built on it; lengths are millimeters unless a unit is written):

FEATURE [PartDesign::FeatureBase] BaseFeature003
  BaseFeature = -> Extrude001
  Suppressed = false
FEATURE [PartDesign::CoordinateSystem] LCS_3
  AttacherType = Attacher::AttachEngine3D
  AttachmentSupport = -> [BaseFeature003]
  MapMode = 2
FEATURE [PartDesign::Body] Body092  label="проставка_корпуса_штока1"
  AllowCompound = false
  BaseFeature = -> Extrude001
  Group = -> [BaseFeature003,LCS_3]
  Origin = -> Origin096
  Tip = -> BaseFeature003
COMPONENT P26 — recipe-attached ("ролик_3*13,8  - 87шт.", modeled in this document).
Construction recipe (the document's own serialized feature program — sketch geometry with constraints, then the solid features built on it; lengths are millimeters unless a unit is written):

FEATURE [PartDesign::AdditiveCylinder] Cylinder
  Angle = 360
  AttacherType = Attacher::AttachEngine3D
  AttachmentOffset = pos=(41.5,0,6.9) rot=(0,0,1;0rad)
  AttachmentSupport = -> [XY_Plane099]
  FirstAngle = 0
  Height = 13.8
  MapMode = 5
  Placement = pos=(41.5,0,6.9) rot=(0,0,1;0rad)
  Radius = 1.5
  Refine = true
  SecondAngle = 0
  Suppressed = false
  expr: .AttachmentOffset.Base.x = <<Dim_table>>.ecc_dia / 2 + 3 / 2
  expr: .AttachmentOffset.Base.z = 13.8 / 2
FEATURE [PartDesign::PolarPattern] PolarPattern
  Angle = 360
  Axis = -> Z_Axis097
  BaseFeature = -> Cylinder
  Mode = 0
  Occurrences = 87
  Offset = 120
  Originals = -> [Cylinder]
  Placement = pos=(41.5,0,6.9) rot=(0,0,1;0rad)
  Refine = true
  Suppressed = false
  TransformMode = 1
FEATURE [PartDesign::CoordinateSystem] LCS_4
  AttacherType = Attacher::AttachEngine3D
  AttachmentSupport = -> [Z_Axis097]
  MapMode = 7
  Placement = pos=(0,0,0) rot=(0,1,0;3.14159rad)
FEATURE [PartDesign::Body] Body094  label="ролик_3*13,8  - 87шт."
  AllowCompound = false
  Group = -> [Cylinder,PolarPattern,LCS_4]
  Origin = -> Origin098
  Tip = -> PolarPattern
COMPONENT P27 — recipe-attached ("Подшипник 943/25", modeled in this document).
Construction recipe (the document's own serialized feature program — sketch geometry with constraints, then the solid features built on it; lengths are millimeters unless a unit is written):

FEATURE [PartDesign::AdditiveCylinder] Cylinder006
  Angle = 360
  AttacherType = Attacher::AttachEngine3D
  FirstAngle = 0
  Height = 25
  MapMode = 2
  Radius = 16
  Refine = true
  SecondAngle = 0
  Suppressed = false
FEATURE [PartDesign::SubtractiveCylinder] Cylinder007
  Angle = 360
  AttacherType = Attacher::AttachEngine3D
  AttachmentSupport = -> [XY_Plane101]
  BaseFeature = -> Cylinder006
  FirstAngle = 0
  Height = 25
  MapMode = 5
  Radius = 12.5
  Refine = true
  SecondAngle = 0
  Suppressed = false
FEATURE [PartDesign::CoordinateSystem] LCS_1
  AttacherType = Attacher::AttachEngine3D
FEATURE [PartDesign::Body] Body095  label="Подшипник 943/25"
  AllowCompound = false
  Group = -> [Cylinder006,Cylinder007,LCS_1]
  Origin = -> Origin100
  Tip = -> Cylinder007
COMPONENT P28 — recipe-attached ("проставка_корпуса_с_шестернями", modeled in this document).
Construction recipe (the document's own serialized feature program — sketch geometry with constraints, then the solid features built on it; lengths are millimeters unless a unit is written):

FEATURE [Sketcher::SketchObject] Sketch075
  ArcFitTolerance = 0
  AttachmentSupport = -> [XY_Plane096]
  FullyConstrained = true
  MakeInternals = false
  MapMode = 5
  expr: Constraints[14] = <<Dim_table>>.inter_shaft_len * 2.15
  expr: Constraints[15] = <<Dim_table>>.ecc_dia * 1.2
  expr: Constraints[16] = <<Dim_table>>.inter_shaft_len * 1.85
  expr: Constraints[22] = <<Dim_table>>.inter_shaft_len / 2
  expr: Constraints[37] = <<Dim_table>>.inter_shaft_len * 2.35
  expr: Constraints[38] = <<Dim_table>>.crank_dia2
  expr: Constraints[39] = <<Dim_table>>.inter_shaft_len * 2
  expr: Constraints[45] = <<Dim_table>>.inter_shaft_len / 2
  expr: Constraints[53] = <<Dim_table>>.axle_hole_dia
  expr: Constraints[56] = <<Dim_table>>.inter_shaft_len
  expr: Constraints[58] = <<Dim_table>>.inter_shaft_len * 0.95
  sketch-geometry (26):
    g0: LineSegment [constr] StartX=-9.5 StartY=-92.5 StartZ=0 EndX=109.5 EndY=-92.5 EndZ=0
    g1: LineSegment [constr] StartX=157.5 StartY=-44.5 StartZ=0 EndX=157.5 EndY=44.5 EndZ=0
    g2: LineSegment [constr] StartX=109.5 StartY=92.5 StartZ=0 EndX=-9.5 EndY=92.5 EndZ=0
    g3: LineSegment [constr] StartX=-57.5 StartY=44.5 StartZ=0 EndX=-57.5 EndY=-44.5 EndZ=0
    g4: ArcOfCircle [constr] CenterX=-9.5 CenterY=44.5 CenterZ=0 NormalX=0 NormalY=0 NormalZ=1 AngleXU=0 Radius=48 StartAngle=1.5708 EndAngle=3.14159
    g5: ArcOfCircle [constr] CenterX=109.5 CenterY=44.5 CenterZ=0 NormalX=0 NormalY=0 NormalZ=1 AngleXU=0 Radius=48 StartAngle=0 EndAngle=1.5708
    g6: ArcOfCircle [constr] CenterX=-9.5 CenterY=-44.5 CenterZ=0 NormalX=0 NormalY=0 NormalZ=1 AngleXU=0 Radius=48 StartAngle=3.14159 EndAngle=4.71239
    g7: ArcOfCircle [constr] CenterX=109.5 CenterY=-44.5 CenterZ=0 NormalX=0 NormalY=0 NormalZ=1 AngleXU=0 Radius=48 StartAngle=4.71239 EndAngle=6.28319
    g8: LineSegment [constr] StartX=-57.5 StartY=-44.5 StartZ=0 EndX=157.5 EndY=44.5 EndZ=0
    g9: GeomPoint [constr] X=50 Y=0 Z=0
    g10: ArcOfCircle CenterX=-55 CenterY=87.5 CenterZ=0 NormalX=0 NormalY=0 NormalZ=1 AngleXU=0 Radius=12.5 StartAngle=1.5708 EndAngle=3.14159
    g11: LineSegment StartX=155 StartY=100 StartZ=0 EndX=-55 EndY=100 EndZ=0
    g12: ArcOfCircle CenterX=155 CenterY=87.5 CenterZ=0 NormalX=0 NormalY=0 NormalZ=1 AngleXU=0 Radius=12.5 StartAngle=7.01e-14 EndAngle=1.5708
    g13: LineSegment StartX=167.5 StartY=-87.5 StartZ=0 EndX=167.5 EndY=87.5 EndZ=0
    g14: ArcOfCircle CenterX=155 CenterY=-87.5 CenterZ=0 NormalX=0 NormalY=0 NormalZ=1 AngleXU=0 Radius=12.5 StartAngle=4.71239 EndAngle=6.28319
    g15: LineSegment StartX=-55 StartY=-100 StartZ=0 EndX=155 EndY=-100 EndZ=0
    g16: ArcOfCircle CenterX=-55 CenterY=-87.5 CenterZ=0 NormalX=0 NormalY=0 NormalZ=1 AngleXU=0 Radius=12.5 StartAngle=3.14159 EndAngle=4.71239
    g17: LineSegment StartX=-67.5 StartY=87.5 StartZ=0 EndX=-67.5 EndY=-87.5 EndZ=0
    g18: LineSegment [constr] StartX=-55 StartY=100 StartZ=0 EndX=155 EndY=-100 EndZ=0
    g19: GeomPoint [constr] X=50 Y=0 Z=0
    g20: Circle CenterX=-55 CenterY=87.5 CenterZ=0 NormalX=0 NormalY=0 NormalZ=1 AngleXU=0 Radius=2.5
    g21: Circle CenterX=155 CenterY=87.5 CenterZ=0 NormalX=0 NormalY=0 NormalZ=1 AngleXU=0 Radius=2.5
    g22: Circle CenterX=-55 CenterY=-87.5 CenterZ=0 NormalX=0 NormalY=0 NormalZ=1 AngleXU=0 Radius=2.5
    g23: Circle CenterX=155 CenterY=-87.5 CenterZ=0 NormalX=0 NormalY=0 NormalZ=1 AngleXU=0 Radius=2.5
    g24: Circle CenterX=0 CenterY=0 CenterZ=0 NormalX=0 NormalY=0 NormalZ=1 AngleXU=0 Radius=47.5
    g25: Circle CenterX=100 CenterY=0 CenterZ=0 NormalX=0 NormalY=0 NormalZ=1 AngleXU=0 Radius=47.5
  constraints (59):
    c: Horizontal(g0)
    c: Horizontal(g2)
    c: Vertical(g1)
    c: Vertical(g3)
    c: Tangent(g2,g4) = -1.5708
    c: Tangent(g3,g4) = -1.5708
    c: Tangent(g2,g5) = -1.5708
    c: Tangent(g1,g5) = -1.5708
    c: Tangent(g3,g6) = -1.5708
    c: Tangent(g0,g6) = -1.5708
    c: Tangent(g0,g7) = -1.5708
    c: Tangent(g1,g7) = -1.5708
    c: Equal(g4,g5)
    c: Equal(g5,g7)
    c: DistanceX(g3,g1) = 215
    c: Diameter(g4) = 96
    c: DistanceY(g0,g2) = 185
    c: Symmetric(g2,g0,g-1)
    c: Coincident(g8,g3)
    c: Coincident(g8,g1)
    c: PointOnObject(g9,g-1)
    c: PointOnObject(g9,g8)
    c: DistanceX(g-1,g9) = 50
    c: Horizontal(g15)
    c: Horizontal(g11)
    c: Vertical(g13)
    c: Vertical(g17)
    c: Tangent(g11,g10) = -1.5708
    c: Tangent(g17,g10) = -1.5708
    c: Tangent(g11,g12) = -1.5708
    c: Tangent(g13,g12) = -1.5708
    c: Tangent(g17,g16) = -1.5708
    c: Tangent(g15,g16) = -1.5708
    c: Tangent(g15,g14) = -1.5708
    c: Tangent(g13,g14) = -1.5708
    c: Equal(g10,g12)
    c: Equal(g12,g14)
    c: DistanceX(g17,g13) = 235
    c: Diameter(g10) = 25
    c: DistanceY(g15,g11) = 200
    c: Symmetric(g10,g16,g-1)
    c: Coincident(g18,g10)
    c: Coincident(g18,g14)
    c: PointOnObject(g19,g-1)
    c: PointOnObject(g19,g18)
    c: DistanceX(g-1,g19) = 50
    c: Coincident(g20,g10)
    c: Coincident(g21,g12)
    c: Coincident(g22,g16)
    c: Coincident(g23,g14)
    c: Equal(g22,g23)
    c: Equal(g23,g21)
    c: Equal(g21,g20)
    c: Diameter(g20) = 5
    c: Coincident(g24,g-1)
    c: PointOnObject(g25,g-1)
    c: DistanceX(g24,g25) = 100
    c: Equal(g25,g24)
    c: Diameter(g24) = 95
FEATURE [Sketcher::SketchObject] Sketch076
  ArcFitTolerance = 0
  AttachmentSupport = -> [XY_Plane096]
  FullyConstrained = true
  MakeInternals = false
  MapMode = 5
  expr: Constraints[14] = <<Dim_table>>.inter_shaft_len * 2.15
  expr: Constraints[15] = <<Dim_table>>.ecc_dia * 1.2
  expr: Constraints[16] = <<Dim_table>>.inter_shaft_len * 1.85
  expr: Constraints[22] = <<Dim_table>>.inter_shaft_len / 2
  expr: Constraints[37] = <<Dim_table>>.inter_shaft_len * 2.35
  expr: Constraints[38] = <<Dim_table>>.crank_dia2
  expr: Constraints[39] = <<Dim_table>>.inter_shaft_len * 2
  expr: Constraints[45] = <<Dim_table>>.inter_shaft_len / 2
  expr: Constraints[53] = <<Dim_table>>.axle_hole_dia
  sketch-geometry (24):
    g0: LineSegment StartX=-9.5 StartY=-92.5 StartZ=0 EndX=109.5 EndY=-92.5 EndZ=0
    g1: LineSegment StartX=157.5 StartY=-44.5 StartZ=0 EndX=157.5 EndY=44.5 EndZ=0
    g2: LineSegment StartX=109.5 StartY=92.5 StartZ=0 EndX=-9.5 EndY=92.5 EndZ=0
    g3: LineSegment StartX=-57.5 StartY=44.5 StartZ=0 EndX=-57.5 EndY=-44.5 EndZ=0
    g4: ArcOfCircle CenterX=-9.5 CenterY=44.5 CenterZ=0 NormalX=0 NormalY=0 NormalZ=1 AngleXU=0 Radius=48 StartAngle=1.5708 EndAngle=3.14159
    g5: ArcOfCircle CenterX=109.5 CenterY=44.5 CenterZ=0 NormalX=0 NormalY=0 NormalZ=1 AngleXU=0 Radius=48 StartAngle=0 EndAngle=1.5708
    g6: ArcOfCircle CenterX=-9.5 CenterY=-44.5 CenterZ=0 NormalX=0 NormalY=0 NormalZ=1 AngleXU=0 Radius=48 StartAngle=3.14159 EndAngle=4.71239
    g7: ArcOfCircle CenterX=109.5 CenterY=-44.5 CenterZ=0 NormalX=0 NormalY=0 NormalZ=1 AngleXU=0 Radius=48 StartAngle=4.71239 EndAngle=6.28319
    g8: LineSegment [constr] StartX=-57.5 StartY=-44.5 StartZ=0 EndX=157.5 EndY=44.5 EndZ=0
    g9: GeomPoint [constr] X=50 Y=0 Z=0
    g10: ArcOfCircle CenterX=-55 CenterY=87.5 CenterZ=0 NormalX=0 NormalY=0 NormalZ=1 AngleXU=0 Radius=12.5 StartAngle=1.5708 EndAngle=3.14159
    g11: LineSegment StartX=155 StartY=100 StartZ=0 EndX=-55 EndY=100 EndZ=0
    g12: ArcOfCircle CenterX=155 CenterY=87.5 CenterZ=0 NormalX=0 NormalY=0 NormalZ=1 AngleXU=0 Radius=12.5 StartAngle=7e-14 EndAngle=1.5708
    g13: LineSegment StartX=167.5 StartY=-87.5 StartZ=0 EndX=167.5 EndY=87.5 EndZ=0
    g14: ArcOfCircle CenterX=155 CenterY=-87.5 CenterZ=0 NormalX=0 NormalY=0 NormalZ=1 AngleXU=0 Radius=12.5 StartAngle=4.71239 EndAngle=6.28319
    g15: LineSegment StartX=-55 StartY=-100 StartZ=0 EndX=155 EndY=-100 EndZ=0
    g16: ArcOfCircle CenterX=-55 CenterY=-87.5 CenterZ=0 NormalX=0 NormalY=0 NormalZ=1 AngleXU=0 Radius=12.5 StartAngle=3.14159 EndAngle=4.71239
    g17: LineSegment StartX=-67.5 StartY=87.5 StartZ=0 EndX=-67.5 EndY=-87.5 EndZ=0
    g18: LineSegment [constr] StartX=-55 StartY=100 StartZ=0 EndX=155 EndY=-100 EndZ=0
    g19: GeomPoint [constr] X=50 Y=0 Z=0
    g20: Circle CenterX=-55 CenterY=87.5 CenterZ=0 NormalX=0 NormalY=0 NormalZ=1 AngleXU=0 Radius=2.5
    g21: Circle CenterX=155 CenterY=87.5 CenterZ=0 NormalX=0 NormalY=0 NormalZ=1 AngleXU=0 Radius=2.5
    g22: Circle CenterX=-55 CenterY=-87.5 CenterZ=0 NormalX=0 NormalY=0 NormalZ=1 AngleXU=0 Radius=2.5
    g23: Circle CenterX=155 CenterY=-87.5 CenterZ=0 NormalX=0 NormalY=0 NormalZ=1 AngleXU=0 Radius=2.5
  constraints (54):
    c: Horizontal(g0)
    c: Horizontal(g2)
    c: Vertical(g1)
    c: Vertical(g3)
    c: Tangent(g2,g4) = -1.5708
    c: Tangent(g3,g4) = -1.5708
    c: Tangent(g2,g5) = -1.5708
    c: Tangent(g1,g5) = -1.5708
    c: Tangent(g3,g6) = -1.5708
    c: Tangent(g0,g6) = -1.5708
    c: Tangent(g0,g7) = -1.5708
    c: Tangent(g1,g7) = -1.5708
    c: Equal(g4,g5)
    c: Equal(g5,g7)
    c: DistanceX(g3,g1) = 215
    c: Diameter(g4) = 96
    c: DistanceY(g0,g2) = 185
    c: Symmetric(g2,g0,g-1)
    c: Coincident(g8,g3)
    c: Coincident(g8,g1)
    c: PointOnObject(g9,g-1)
    c: PointOnObject(g9,g8)
    c: DistanceX(g-1,g9) = 50
    c: Horizontal(g15)
    c: Horizontal(g11)
    c: Vertical(g13)
    c: Vertical(g17)
    c: Tangent(g11,g10) = -1.5708
    c: Tangent(g17,g10) = -1.5708
    c: Tangent(g11,g12) = -1.5708
    c: Tangent(g13,g12) = -1.5708
    c: Tangent(g17,g16) = -1.5708
    c: Tangent(g15,g16) = -1.5708
    c: Tangent(g15,g14) = -1.5708
    c: Tangent(g13,g14) = -1.5708
    c: Equal(g10,g12)
    c: Equal(g12,g14)
    c: DistanceX(g17,g13) = 235
    c: Diameter(g10) = 25
    c: DistanceY(g15,g11) = 200
    c: Symmetric(g10,g16,g-1)
    c: Coincident(g18,g10)
    c: Coincident(g18,g14)
    c: PointOnObject(g19,g-1)
    c: PointOnObject(g19,g18)
    c: DistanceX(g-1,g19) = 50
    c: Coincident(g20,g10)
    c: Coincident(g21,g12)
    c: Coincident(g22,g16)
    c: Coincident(g23,g14)
    c: Equal(g22,g23)
    c: Equal(g23,g21)
    c: Equal(g21,g20)
    c: Diameter(g20) = 5
FEATURE [PartDesign::CoordinateSystem] LCS_Origin007
  AttacherType = Attacher::AttachEngine3D
  AttachmentSupport = -> [X_Axis094]
  MapMode = 2
FEATURE [PartDesign::Pad] Pad044
  Direction = (0,0,1)
  Length = 6
  Length2 = 10
  Profile = -> Sketch075
  ReferenceAxis = -> Sketch075 [N_Axis]
  Suppressed = false
  Type = 0
FEATURE [PartDesign::Pad] Pad045
  BaseFeature = -> Pad044
  Direction = (0,0,1)
  Length = 16.75
  Length2 = 10
  Profile = -> Sketch076
  ReferenceAxis = -> Sketch076 [N_Axis]
  Suppressed = false
  Type = 0
FEATURE [PartDesign::Body] Body_2  label="проставка_корпуса_с_шестернями"
  AllowCompound = false
  Group = -> [LCS_Origin007,Sketch075,Pad044,Sketch076,Pad045]
  Origin = -> Origin095
  Tip = -> Pad045
COMPONENT P29 — recipe-attached ("ролик 3х21.8", modeled in this document).
Construction recipe (the document's own serialized feature program — sketch geometry with constraints, then the solid features built on it; lengths are millimeters unless a unit is written):

FEATURE [PartDesign::CoordinateSystem] LCS_Origin008
  AttacherType = Attacher::AttachEngine3D
  AttachmentSupport = -> [X_Axis098]
  MapMode = 2
FEATURE [PartDesign::AdditiveCylinder] Cylinder001
  Angle = 360
  AttacherType = Attacher::AttachEngine3D
  FirstAngle = 0
  Height = 21.8
  MapMode = 1
  Radius = 1.5
  Refine = true
  SecondAngle = 0
  Suppressed = false
FEATURE [PartDesign::Body] ___________3__21_8  label="ролик 3х21.8"
  AllowCompound = false
  Group = -> [LCS_Origin008,Cylinder001]
  Origin = -> Origin099
  Tip = -> Cylinder001
COMPONENT P30 — recipe-attached ("корпус_верхний", modeled in this document).
Construction recipe (the document's own serialized feature program — sketch geometry with constraints, then the solid features built on it; lengths are millimeters unless a unit is written):

FEATURE [Sketcher::SketchObject] Sketch067
  ArcFitTolerance = 0
  AttachmentSupport = -> [XY_Plane085]
  FullyConstrained = true
  MakeInternals = false
  MapMode = 5
  expr: Constraints[14] = <<Dim_table>>.inter_shaft_len * 2.15
  expr: Constraints[15] = <<Dim_table>>.ecc_dia * 1.2
  expr: Constraints[16] = <<Dim_table>>.inter_shaft_len * 1.85
  expr: Constraints[22] = <<Dim_table>>.inter_shaft_len / 2
  expr: Constraints[37] = <<Dim_table>>.inter_shaft_len * 2.35
  expr: Constraints[38] = <<Dim_table>>.crank_dia2
  expr: Constraints[39] = <<Dim_table>>.inter_shaft_len * 2
  expr: Constraints[45] = <<Dim_table>>.inter_shaft_len / 2
  expr: Constraints[53] = <<Dim_table>>.axle_hole_dia
  expr: Constraints[56] = <<Dim_table>>.inter_shaft_len
  expr: Constraints[58] = <<Dim_table>>.crank_dia2 + <<Dim_table>>.zazor
  sketch-geometry (27):
    g0: LineSegment [constr] StartX=-9.5 StartY=-92.5 StartZ=0 EndX=109.5 EndY=-92.5 EndZ=0
    g1: LineSegment [constr] StartX=157.5 StartY=-44.5 StartZ=0 EndX=157.5 EndY=44.5 EndZ=0
    g2: LineSegment [constr] StartX=109.5 StartY=92.5 StartZ=0 EndX=-9.5 EndY=92.5 EndZ=0
    g3: LineSegment [constr] StartX=-57.5 StartY=44.5 StartZ=0 EndX=-57.5 EndY=-44.5 EndZ=0
    g4: ArcOfCircle [constr] CenterX=-9.5 CenterY=44.5 CenterZ=0 NormalX=0 NormalY=0 NormalZ=1 AngleXU=0 Radius=48 StartAngle=1.5708 EndAngle=3.14159
    g5: ArcOfCircle [constr] CenterX=109.5 CenterY=44.5 CenterZ=0 NormalX=0 NormalY=0 NormalZ=1 AngleXU=0 Radius=48 StartAngle=0 EndAngle=1.5708
    g6: ArcOfCircle [constr] CenterX=-9.5 CenterY=-44.5 CenterZ=0 NormalX=0 NormalY=0 NormalZ=1 AngleXU=0 Radius=48 StartAngle=3.14159 EndAngle=4.71239
    g7: ArcOfCircle [constr] CenterX=109.5 CenterY=-44.5 CenterZ=0 NormalX=0 NormalY=0 NormalZ=1 AngleXU=0 Radius=48 StartAngle=4.71239 EndAngle=6.28319
    g8: LineSegment [constr] StartX=-57.5 StartY=-44.5 StartZ=0 EndX=157.5 EndY=44.5 EndZ=0
    g9: GeomPoint [constr] X=50 Y=0 Z=0
    g10: ArcOfCircle CenterX=-55 CenterY=87.5 CenterZ=0 NormalX=0 NormalY=0 NormalZ=1 AngleXU=0 Radius=12.5 StartAngle=1.5708 EndAngle=3.14159
    g11: LineSegment StartX=155 StartY=100 StartZ=0 EndX=-55 EndY=100 EndZ=0
    g12: ArcOfCircle CenterX=155 CenterY=87.5 CenterZ=0 NormalX=0 NormalY=0 NormalZ=1 AngleXU=0 Radius=12.5 StartAngle=7.02e-14 EndAngle=1.5708
    g13: LineSegment StartX=167.5 StartY=-87.5 StartZ=0 EndX=167.5 EndY=87.5 EndZ=0
    g14: ArcOfCircle CenterX=155 CenterY=-87.5 CenterZ=0 NormalX=0 NormalY=0 NormalZ=1 AngleXU=0 Radius=12.5 StartAngle=4.71239 EndAngle=6.28319
    g15: LineSegment StartX=-55 StartY=-100 StartZ=0 EndX=155 EndY=-100 EndZ=0
    g16: ArcOfCircle CenterX=-55 CenterY=-87.5 CenterZ=0 NormalX=0 NormalY=0 NormalZ=1 AngleXU=0 Radius=12.5 StartAngle=3.14159 EndAngle=4.71239
    g17: LineSegment StartX=-67.5 StartY=87.5 StartZ=0 EndX=-67.5 EndY=-87.5 EndZ=0
    g18: LineSegment [constr] StartX=-55 StartY=100 StartZ=0 EndX=155 EndY=-100 EndZ=0
    g19: GeomPoint [constr] X=50 Y=0 Z=0
    g20: Circle CenterX=-55 CenterY=87.5 CenterZ=0 NormalX=0 NormalY=0 NormalZ=1 AngleXU=0 Radius=2.5
    g21: Circle CenterX=155 CenterY=87.5 CenterZ=0 NormalX=0 NormalY=0 NormalZ=1 AngleXU=0 Radius=2.5
    g22: Circle CenterX=-55 CenterY=-87.5 CenterZ=0 NormalX=0 NormalY=0 NormalZ=1 AngleXU=0 Radius=2.5
    g23: Circle CenterX=155 CenterY=-87.5 CenterZ=0 NormalX=0 NormalY=0 NormalZ=1 AngleXU=0 Radius=2.5
    g24: Circle CenterX=0 CenterY=0 CenterZ=0 NormalX=0 NormalY=0 NormalZ=1 AngleXU=0 Radius=12.75
    g25: Circle CenterX=100 CenterY=0 CenterZ=0 NormalX=0 NormalY=0 NormalZ=1 AngleXU=0 Radius=12.75
    g26: Circle CenterX=50 CenterY=0 CenterZ=0 NormalX=0 NormalY=0 NormalZ=1 AngleXU=0 Radius=12.75
  constraints (61):
    c: Horizontal(g0)
    c: Horizontal(g2)
    c: Vertical(g1)
    c: Vertical(g3)
    c: Tangent(g2,g4) = -1.5708
    c: Tangent(g3,g4) = -1.5708
    c: Tangent(g2,g5) = -1.5708
    c: Tangent(g1,g5) = -1.5708
    c: Tangent(g3,g6) = -1.5708
    c: Tangent(g0,g6) = -1.5708
    c: Tangent(g0,g7) = -1.5708
    c: Tangent(g1,g7) = -1.5708
    c: Equal(g4,g5)
    c: Equal(g5,g7)
    c: DistanceX(g3,g1) = 215
    c: Diameter(g4) = 96
    c: DistanceY(g0,g2) = 185
    c: Symmetric(g2,g0,g-1)
    c: Coincident(g8,g3)
    c: Coincident(g8,g1)
    c: PointOnObject(g9,g-1)
    c: PointOnObject(g9,g8)
    c: DistanceX(g-1,g9) = 50
    c: Horizontal(g15)
    c: Horizontal(g11)
    c: Vertical(g13)
    c: Vertical(g17)
    c: Tangent(g11,g10) = -1.5708
    c: Tangent(g17,g10) = -1.5708
    c: Tangent(g11,g12) = -1.5708
    c: Tangent(g13,g12) = -1.5708
    c: Tangent(g17,g16) = -1.5708
    c: Tangent(g15,g16) = -1.5708
    c: Tangent(g15,g14) = -1.5708
    c: Tangent(g13,g14) = -1.5708
    c: Equal(g10,g12)
    c: Equal(g12,g14)
    c: DistanceX(g17,g13) = 235
    c: Diameter(g10) = 25
    c: DistanceY(g15,g11) = 200
    c: Symmetric(g10,g16,g-1)
    c: Coincident(g18,g10)
    c: Coincident(g18,g14)
    c: PointOnObject(g19,g-1)
    c: PointOnObject(g19,g18)
    c: DistanceX(g-1,g19) = 50
    c: Coincident(g20,g10)
    c: Coincident(g21,g12)
    c: Coincident(g22,g16)
    c: Coincident(g23,g14)
    c: Equal(g22,g23)
    c: Equal(g23,g21)
    c: Equal(g21,g20)
    c: Diameter(g20) = 5
    c: Coincident(g24,g-1)
    c: PointOnObject(g25,g-1)
    c: DistanceX(g24,g25) = 100
    c: Equal(g25,g24)
    c: Diameter(g24) = 25.5
    c: Coincident(g26,g9)
    c: Equal(g24,g26)
FEATURE [PartDesign::CoordinateSystem] LCS_Origin006
  AttacherType = Attacher::AttachEngine3D
  AttachmentSupport = -> [X_Axis083]
  MapMode = 2
FEATURE [PartDesign::Pad] Pad036
  Direction = (0,0,1)
  Length = 4
  Length2 = 10
  Profile = -> Sketch067
  ReferenceAxis = -> Sketch067 [N_Axis]
  Suppressed = false
  Type = 0
FEATURE [Sketcher::SketchObject] Sketch073
  ArcFitTolerance = 0
  AttachmentSupport = -> [XY_Plane085]
  FullyConstrained = true
  MakeInternals = false
  MapMode = 5
  expr: Constraints[6] = <<Dim_table>>.crank_dia2 + <<Dim_table>>.zazor
  expr: Constraints[7] = <<Dim_table>>.crank_dia2 * 1.5
  expr: Constraints[8] = <<Dim_table>>.inter_shaft_len
  sketch-geometry (4):
    g0: Circle CenterX=0 CenterY=0 CenterZ=0 NormalX=0 NormalY=0 NormalZ=1 AngleXU=0 Radius=12.75
    g1: Circle CenterX=0 CenterY=0 CenterZ=0 NormalX=0 NormalY=0 NormalZ=1 AngleXU=0 Radius=18.75
    g2: Circle CenterX=100 CenterY=0 CenterZ=0 NormalX=0 NormalY=0 NormalZ=1 AngleXU=0 Radius=12.75
    g3: Circle CenterX=100 CenterY=0 CenterZ=0 NormalX=0 NormalY=0 NormalZ=1 AngleXU=0 Radius=18.75
  constraints (9):
    c: Coincident(g0,g-1)
    c: Coincident(g1,g0)
    c: PointOnObject(g2,g-1)
    c: Coincident(g3,g2)
    c: Equal(g0,g2)
    c: Equal(g1,g3)
    c: Diameter(g0) = 25.5
    c: Diameter(g1) = 37.5
    c: DistanceX(g-1,g2) = 100
FEATURE [PartDesign::Pad] Pad041
  BaseFeature = -> Pad036
  Direction = (0,0,1)
  Length = 10
  Length2 = 10
  Profile = -> Sketch073
  ReferenceAxis = -> Sketch073 [N_Axis]
  Suppressed = false
  Type = 0
FEATURE [PartDesign::Body] ___________________________  label="корпус_верхний"
  AllowCompound = false
  Group = -> [LCS_Origin006,Sketch067,Pad036,Sketch073,Pad041]
  Origin = -> Origin084
  Tip = -> Pad041
PROVENANCE & LICENSES
A FreeCAD (.FCStd) document from a public repository crawl; recipes are the document's own serialized feature recipes (and, for linked parts, companion documents' recipes).
License: unknown-license-file.
